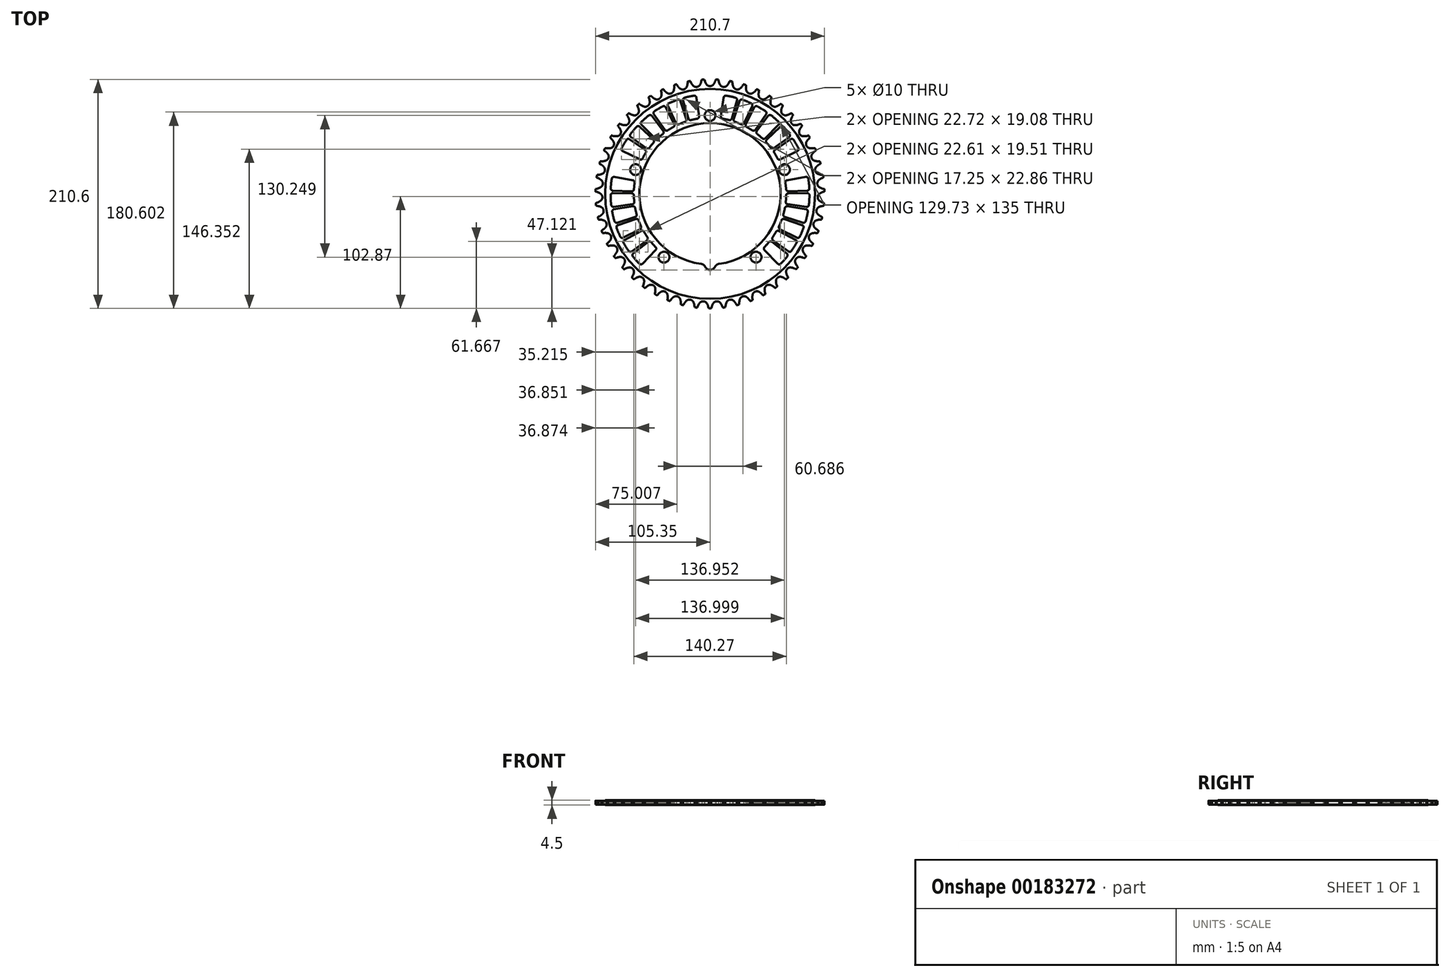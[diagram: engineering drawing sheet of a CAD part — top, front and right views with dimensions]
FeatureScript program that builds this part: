
annotation { "Feature Type Name" : "Feature", "Feature Type Description" : "" }
export const myFeature = defineFeature(function(context is Context, id is Id, definition is map)
    precondition{}
    {
        {
            var Q0;
            Q0=qCreatedBy(makeId("Top.planeOp"),FACE);
            var sketch = newSketch(context, id + "F0", { "sketchPlane" : qUnion([Q0])});
            skCircle(sketch, "E0", {"center": v(0, 0) * mm, "radius": 103.08 * mm, "construction": true});
            skArc(sketch, "E1", {"start": v(-4.68, 103.4) * mm, "mid": v(-4.06, 102) * mm, "end": v(-3.24, 100.71) * mm});
            skLineSegment(sketch, "E2", {"start": v(-4.68, 103.4) * mm, "end": v(-5.06, 104.51) * mm});
            skArc(sketch, "E3.trimOffspring", {"start": v(-5.06, 104.51) * mm, "mid": v(-5.7, 105.82) * mm, "end": v(-6.6, 106.94) * mm});
            skLineSegment(sketch, "E4.trimOffspring", {"start": v(0, 103.08) * mm, "end": v(0, 103.08) * mm});
            skArc(sketch, "E5.trimOffspring", {"start": v(-3.24, 100.71) * mm, "mid": v(-1.82, 99.5) * mm, "end": v(0, 99.07) * mm});
            skArc(sketch, "E6.MirrorCS", {"start": v(3.24, 100.71) * mm, "mid": v(1.82, 99.5) * mm, "end": v(0, 99.07) * mm});
            skArc(sketch, "E7.MirrorCS", {"start": v(4.68, 103.4) * mm, "mid": v(4.06, 102) * mm, "end": v(3.24, 100.71) * mm});
            skLineSegment(sketch, "E8.MirrorCS", {"start": v(4.68, 103.4) * mm, "end": v(5.06, 104.51) * mm});
            skArc(sketch, "E9.MirrorCS", {"start": v(5.06, 104.51) * mm, "mid": v(5.7, 105.82) * mm, "end": v(6.6, 106.94) * mm});
            skArc(sketch, "E10.1.0", {"start": v(-17.87, 103.1) * mm, "mid": v(-18.65, 104.31) * mm, "end": v(-19.69, 105.32) * mm});
            skLineSegment(sketch, "E10.1.1", {"start": v(-17.35, 102.05) * mm, "end": v(-17.87, 103.1) * mm});
            skArc(sketch, "E10.1.2", {"start": v(-17.35, 102.05) * mm, "mid": v(-16.56, 100.74) * mm, "end": v(-15.6, 99.55) * mm});
            skArc(sketch, "E10.1.3", {"start": v(-15.6, 99.55) * mm, "mid": v(-14.03, 98.53) * mm, "end": v(-12.17, 98.32) * mm});
            skArc(sketch, "E10.1.4", {"start": v(-9.16, 100.35) * mm, "mid": v(-10.42, 98.97) * mm, "end": v(-12.17, 98.32) * mm});
            skArc(sketch, "E10.1.5", {"start": v(-8.07, 103.2) * mm, "mid": v(-8.5, 101.73) * mm, "end": v(-9.16, 100.35) * mm});
            skLineSegment(sketch, "E10.1.6", {"start": v(-8.07, 103.2) * mm, "end": v(-7.82, 104.34) * mm});
            skArc(sketch, "E10.1.7", {"start": v(-7.82, 104.34) * mm, "mid": v(-7.36, 105.71) * mm, "end": v(-6.6, 106.94) * mm});
            skArc(sketch, "E10.2.0", {"start": v(-30.4, 100.12) * mm, "mid": v(-31.33, 101.23) * mm, "end": v(-32.48, 102.1) * mm});
            skLineSegment(sketch, "E10.2.1", {"start": v(-29.76, 99.14) * mm, "end": v(-30.4, 100.12) * mm});
            skArc(sketch, "E10.2.2", {"start": v(-29.76, 99.14) * mm, "mid": v(-28.82, 97.94) * mm, "end": v(-27.7, 96.88) * mm});
            skArc(sketch, "E10.2.3", {"start": v(-27.7, 96.88) * mm, "mid": v(-26.03, 96.06) * mm, "end": v(-24.16, 96.08) * mm});
            skArc(sketch, "E10.2.4", {"start": v(-21.42, 98.46) * mm, "mid": v(-22.5, 96.94) * mm, "end": v(-24.16, 96.08) * mm});
            skArc(sketch, "E10.2.5", {"start": v(-20.69, 101.43) * mm, "mid": v(-20.95, 99.92) * mm, "end": v(-21.42, 98.46) * mm});
            skLineSegment(sketch, "E10.2.6", {"start": v(-20.69, 101.43) * mm, "end": v(-20.58, 102.6) * mm});
            skArc(sketch, "E10.2.7", {"start": v(-20.58, 102.6) * mm, "mid": v(-20.3, 104) * mm, "end": v(-19.69, 105.32) * mm});
            skArc(sketch, "E10.3.0", {"start": v(-42.48, 95.63) * mm, "mid": v(-43.53, 96.61) * mm, "end": v(-44.78, 97.34) * mm});
            skLineSegment(sketch, "E10.3.1", {"start": v(-41.72, 94.74) * mm, "end": v(-42.48, 95.63) * mm});
            skArc(sketch, "E10.3.2", {"start": v(-41.72, 94.74) * mm, "mid": v(-40.63, 93.65) * mm, "end": v(-39.4, 92.74) * mm});
            skArc(sketch, "E10.3.3", {"start": v(-39.4, 92.74) * mm, "mid": v(-37.64, 92.13) * mm, "end": v(-35.79, 92.38) * mm});
            skArc(sketch, "E10.3.4", {"start": v(-33.36, 95.08) * mm, "mid": v(-34.25, 93.44) * mm, "end": v(-35.79, 92.38) * mm});
            skArc(sketch, "E10.3.5", {"start": v(-33, 98.11) * mm, "mid": v(-33.07, 96.59) * mm, "end": v(-33.36, 95.08) * mm});
            skLineSegment(sketch, "E10.3.6", {"start": v(-33, 98.11) * mm, "end": v(-33.03, 99.29) * mm});
            skArc(sketch, "E10.3.7", {"start": v(-33.03, 99.29) * mm, "mid": v(-32.92, 100.73) * mm, "end": v(-32.48, 102.1) * mm});
            skArc(sketch, "E10.4.0", {"start": v(-53.9, 89.68) * mm, "mid": v(-55.08, 90.53) * mm, "end": v(-56.4, 91.1) * mm});
            skLineSegment(sketch, "E10.4.1", {"start": v(-53.04, 88.9) * mm, "end": v(-53.9, 89.68) * mm});
            skArc(sketch, "E10.4.2", {"start": v(-53.04, 88.9) * mm, "mid": v(-51.83, 87.95) * mm, "end": v(-50.5, 87.2) * mm});
            skArc(sketch, "E10.4.3", {"start": v(-50.5, 87.2) * mm, "mid": v(-48.68, 86.8) * mm, "end": v(-46.87, 87.28) * mm});
            skArc(sketch, "E10.4.4", {"start": v(-44.8, 90.26) * mm, "mid": v(-45.47, 88.52) * mm, "end": v(-46.87, 87.28) * mm});
            skArc(sketch, "E10.4.5", {"start": v(-44.8, 93.32) * mm, "mid": v(-44.68, 91.8) * mm, "end": v(-44.8, 90.26) * mm});
            skLineSegment(sketch, "E10.4.6", {"start": v(-44.8, 93.32) * mm, "end": v(-44.98, 94.47) * mm});
            skArc(sketch, "E10.4.7", {"start": v(-44.98, 94.47) * mm, "mid": v(-45.05, 95.92) * mm, "end": v(-44.78, 97.34) * mm});
            skArc(sketch, "E10.5.0", {"start": v(-64.52, 82.38) * mm, "mid": v(-65.78, 83.08) * mm, "end": v(-67.17, 83.48) * mm});
            skLineSegment(sketch, "E10.5.1", {"start": v(-63.56, 81.7) * mm, "end": v(-64.52, 82.38) * mm});
            skArc(sketch, "E10.5.2", {"start": v(-63.56, 81.7) * mm, "mid": v(-62.25, 80.91) * mm, "end": v(-60.84, 80.33) * mm});
            skArc(sketch, "E10.5.3", {"start": v(-60.84, 80.33) * mm, "mid": v(-58.97, 80.17) * mm, "end": v(-57.24, 80.86) * mm});
            skArc(sketch, "E10.5.4", {"start": v(-55.54, 84.08) * mm, "mid": v(-56, 82.27) * mm, "end": v(-57.24, 80.86) * mm});
            skArc(sketch, "E10.5.5", {"start": v(-55.93, 87.1) * mm, "mid": v(-55.63, 85.6) * mm, "end": v(-55.54, 84.08) * mm});
            skLineSegment(sketch, "E10.5.6", {"start": v(-55.93, 87.1) * mm, "end": v(-56.25, 88.23) * mm});
            skArc(sketch, "E10.5.7", {"start": v(-56.25, 88.23) * mm, "mid": v(-56.5, 89.66) * mm, "end": v(-56.4, 91.1) * mm});
            skArc(sketch, "E10.6.0", {"start": v(-74.15, 73.83) * mm, "mid": v(-75.5, 74.36) * mm, "end": v(-76.92, 74.59) * mm});
            skLineSegment(sketch, "E10.6.1", {"start": v(-73.12, 73.27) * mm, "end": v(-74.15, 73.83) * mm});
            skArc(sketch, "E10.6.2", {"start": v(-73.12, 73.27) * mm, "mid": v(-71.72, 72.65) * mm, "end": v(-70.25, 72.25) * mm});
            skArc(sketch, "E10.6.3", {"start": v(-70.25, 72.25) * mm, "mid": v(-68.38, 72.31) * mm, "end": v(-66.74, 73.21) * mm});
            skArc(sketch, "E10.6.4", {"start": v(-65.46, 76.61) * mm, "mid": v(-65.7, 74.76) * mm, "end": v(-66.74, 73.21) * mm});
            skArc(sketch, "E10.6.5", {"start": v(-66.2, 79.57) * mm, "mid": v(-65.72, 78.12) * mm, "end": v(-65.46, 76.61) * mm});
            skLineSegment(sketch, "E10.6.6", {"start": v(-66.2, 79.57) * mm, "end": v(-66.67, 80.65) * mm});
            skArc(sketch, "E10.6.7", {"start": v(-66.67, 80.65) * mm, "mid": v(-67.08, 82.03) * mm, "end": v(-67.17, 83.48) * mm});
            skArc(sketch, "E10.7.0", {"start": v(-82.66, 64.15) * mm, "mid": v(-84.06, 64.52) * mm, "end": v(-85.5, 64.57) * mm});
            skLineSegment(sketch, "E10.7.1", {"start": v(-81.57, 63.73) * mm, "end": v(-82.66, 64.15) * mm});
            skArc(sketch, "E10.7.2", {"start": v(-81.57, 63.73) * mm, "mid": v(-80.1, 63.29) * mm, "end": v(-78.6, 63.07) * mm});
            skArc(sketch, "E10.7.3", {"start": v(-78.6, 63.07) * mm, "mid": v(-76.75, 63.36) * mm, "end": v(-75.23, 64.46) * mm});
            skArc(sketch, "E10.7.4", {"start": v(-74.37, 67.99) * mm, "mid": v(-74.38, 66.12) * mm, "end": v(-75.23, 64.46) * mm});
            skArc(sketch, "E10.7.5", {"start": v(-75.49, 70.83) * mm, "mid": v(-74.83, 69.45) * mm, "end": v(-74.37, 67.99) * mm});
            skLineSegment(sketch, "E10.7.6", {"start": v(-75.49, 70.83) * mm, "end": v(-76.07, 71.84) * mm});
            skArc(sketch, "E10.7.7", {"start": v(-76.07, 71.84) * mm, "mid": v(-76.65, 73.17) * mm, "end": v(-76.92, 74.59) * mm});
            skArc(sketch, "E10.8.0", {"start": v(-89.92, 53.5) * mm, "mid": v(-91.35, 53.7) * mm, "end": v(-92.8, 53.57) * mm});
            skLineSegment(sketch, "E10.8.1", {"start": v(-88.78, 53.22) * mm, "end": v(-89.92, 53.5) * mm});
            skArc(sketch, "E10.8.2", {"start": v(-88.78, 53.22) * mm, "mid": v(-87.28, 52.96) * mm, "end": v(-85.75, 52.93) * mm});
            skArc(sketch, "E10.8.3", {"start": v(-85.75, 52.93) * mm, "mid": v(-83.95, 53.45) * mm, "end": v(-82.58, 54.72) * mm});
            skArc(sketch, "E10.8.4", {"start": v(-82.17, 58.33) * mm, "mid": v(-81.94, 56.48) * mm, "end": v(-82.58, 54.72) * mm});
            skArc(sketch, "E10.8.5", {"start": v(-83.62, 61.02) * mm, "mid": v(-82.8, 59.73) * mm, "end": v(-82.17, 58.33) * mm});
            skLineSegment(sketch, "E10.8.6", {"start": v(-83.62, 61.02) * mm, "end": v(-84.33, 61.95) * mm});
            skArc(sketch, "E10.8.7", {"start": v(-84.33, 61.95) * mm, "mid": v(-85.06, 63.2) * mm, "end": v(-85.5, 64.57) * mm});
            skArc(sketch, "E10.9.0", {"start": v(-95.81, 42.05) * mm, "mid": v(-97.26, 42.07) * mm, "end": v(-98.67, 41.76) * mm});
            skLineSegment(sketch, "E10.9.1", {"start": v(-94.65, 41.9) * mm, "end": v(-95.81, 42.05) * mm});
            skArc(sketch, "E10.9.2", {"start": v(-94.65, 41.9) * mm, "mid": v(-93.12, 41.84) * mm, "end": v(-91.6, 42) * mm});
            skArc(sketch, "E10.9.3", {"start": v(-91.6, 42) * mm, "mid": v(-89.88, 42.73) * mm, "end": v(-88.68, 44.16) * mm});
            skArc(sketch, "E10.9.4", {"start": v(-88.71, 47.8) * mm, "mid": v(-88.26, 45.98) * mm, "end": v(-88.68, 44.16) * mm});
            skArc(sketch, "E10.9.5", {"start": v(-90.48, 50.28) * mm, "mid": v(-89.5, 49.1) * mm, "end": v(-88.71, 47.8) * mm});
            skLineSegment(sketch, "E10.9.6", {"start": v(-90.48, 50.28) * mm, "end": v(-91.3, 51.12) * mm});
            skArc(sketch, "E10.9.7", {"start": v(-91.3, 51.12) * mm, "mid": v(-92.19, 52.26) * mm, "end": v(-92.8, 53.57) * mm});
            skArc(sketch, "E10.10.0", {"start": v(-100.26, 29.96) * mm, "mid": v(-101.7, 29.8) * mm, "end": v(-103.06, 29.32) * mm});
            skLineSegment(sketch, "E10.10.1", {"start": v(-99.08, 29.96) * mm, "end": v(-100.26, 29.96) * mm});
            skArc(sketch, "E10.10.2", {"start": v(-99.08, 29.96) * mm, "mid": v(-97.56, 30.08) * mm, "end": v(-96.07, 30.42) * mm});
            skArc(sketch, "E10.10.3", {"start": v(-96.07, 30.42) * mm, "mid": v(-94.45, 31.36) * mm, "end": v(-93.44, 32.93) * mm});
            skArc(sketch, "E10.10.4", {"start": v(-93.91, 36.53) * mm, "mid": v(-93.24, 34.78) * mm, "end": v(-93.44, 32.93) * mm});
            skArc(sketch, "E10.10.5", {"start": v(-95.98, 38.78) * mm, "mid": v(-94.86, 37.73) * mm, "end": v(-93.91, 36.53) * mm});
            skLineSegment(sketch, "E10.10.6", {"start": v(-95.98, 38.78) * mm, "end": v(-96.89, 39.51) * mm});
            skArc(sketch, "E10.10.7", {"start": v(-96.89, 39.51) * mm, "mid": v(-97.9, 40.54) * mm, "end": v(-98.67, 41.76) * mm});
            skArc(sketch, "E10.11.0", {"start": v(-103.18, 17.41) * mm, "mid": v(-104.58, 17.08) * mm, "end": v(-105.88, 16.44) * mm});
            skLineSegment(sketch, "E10.11.1", {"start": v(-102.01, 17.55) * mm, "end": v(-103.18, 17.41) * mm});
            skArc(sketch, "E10.11.2", {"start": v(-102.01, 17.55) * mm, "mid": v(-100.51, 17.86) * mm, "end": v(-99.08, 18.38) * mm});
            skArc(sketch, "E10.11.3", {"start": v(-99.08, 18.38) * mm, "mid": v(-97.59, 19.51) * mm, "end": v(-96.78, 21.2) * mm});
            skArc(sketch, "E10.11.4", {"start": v(-97.69, 24.71) * mm, "mid": v(-96.81, 23.06) * mm, "end": v(-96.78, 21.2) * mm});
            skArc(sketch, "E10.11.5", {"start": v(-100.01, 26.7) * mm, "mid": v(-98.78, 25.79) * mm, "end": v(-97.69, 24.71) * mm});
            skLineSegment(sketch, "E10.11.6", {"start": v(-100.01, 26.7) * mm, "end": v(-101.01, 27.3) * mm});
            skArc(sketch, "E10.11.7", {"start": v(-101.01, 27.3) * mm, "mid": v(-102.15, 28.2) * mm, "end": v(-103.06, 29.32) * mm});
            skArc(sketch, "E10.12.0", {"start": v(-104.54, 4.6) * mm, "mid": v(-105.89, 4.1) * mm, "end": v(-107.1, 3.3) * mm});
            skLineSegment(sketch, "E10.12.1", {"start": v(-103.4, 4.88) * mm, "end": v(-104.54, 4.6) * mm});
            skArc(sketch, "E10.12.2", {"start": v(-103.4, 4.88) * mm, "mid": v(-101.95, 5.37) * mm, "end": v(-100.58, 6.07) * mm});
            skArc(sketch, "E10.12.3", {"start": v(-100.58, 6.07) * mm, "mid": v(-99.25, 7.37) * mm, "end": v(-98.65, 9.14) * mm});
            skArc(sketch, "E10.12.4", {"start": v(-99.99, 12.52) * mm, "mid": v(-98.91, 11) * mm, "end": v(-98.65, 9.14) * mm});
            skArc(sketch, "E10.12.5", {"start": v(-102.54, 14.2) * mm, "mid": v(-101.2, 13.45) * mm, "end": v(-99.99, 12.52) * mm});
            skLineSegment(sketch, "E10.12.6", {"start": v(-102.54, 14.2) * mm, "end": v(-103.6, 14.69) * mm});
            skArc(sketch, "E10.12.7", {"start": v(-103.6, 14.69) * mm, "mid": v(-104.84, 15.43) * mm, "end": v(-105.88, 16.44) * mm});
            skArc(sketch, "E10.13.0", {"start": v(-104.3, -8.28) * mm, "mid": v(-105.6, -8.95) * mm, "end": v(-106.7, -9.89) * mm});
            skLineSegment(sketch, "E10.13.1", {"start": v(-103.22, -7.86) * mm, "end": v(-104.3, -8.28) * mm});
            skArc(sketch, "E10.13.2", {"start": v(-103.22, -7.86) * mm, "mid": v(-101.84, -7.2) * mm, "end": v(-100.57, -6.34) * mm});
            skArc(sketch, "E10.13.3", {"start": v(-100.57, -6.34) * mm, "mid": v(-99.4, -4.88) * mm, "end": v(-99.02, -3.05) * mm});
            skArc(sketch, "E10.13.4", {"start": v(-100.77, 0.14) * mm, "mid": v(-99.51, -1.25) * mm, "end": v(-99.02, -3.05) * mm});
            skArc(sketch, "E10.13.5", {"start": v(-103.5, 1.5) * mm, "mid": v(-102.08, 0.92) * mm, "end": v(-100.77, 0.14) * mm});
            skLineSegment(sketch, "E10.13.6", {"start": v(-103.5, 1.5) * mm, "end": v(-104.62, 1.84) * mm});
            skArc(sketch, "E10.13.7", {"start": v(-104.62, 1.84) * mm, "mid": v(-105.94, 2.43) * mm, "end": v(-107.1, 3.3) * mm});
            skArc(sketch, "E10.14.0", {"start": v(-102.5, -21.03) * mm, "mid": v(-103.7, -21.86) * mm, "end": v(-104.67, -22.92) * mm});
            skLineSegment(sketch, "E10.14.1", {"start": v(-101.47, -20.48) * mm, "end": v(-102.5, -21.03) * mm});
            skArc(sketch, "E10.14.2", {"start": v(-101.47, -20.48) * mm, "mid": v(-100.18, -19.66) * mm, "end": v(-99.03, -18.65) * mm});
            skArc(sketch, "E10.14.3", {"start": v(-99.03, -18.65) * mm, "mid": v(-98.05, -17.06) * mm, "end": v(-97.9, -15.2) * mm});
            skArc(sketch, "E10.14.4", {"start": v(-100.02, -12.25) * mm, "mid": v(-98.6, -13.47) * mm, "end": v(-97.9, -15.2) * mm});
            skArc(sketch, "E10.14.5", {"start": v(-102.9, -11.24) * mm, "mid": v(-101.42, -11.64) * mm, "end": v(-100.02, -12.25) * mm});
            skLineSegment(sketch, "E10.14.6", {"start": v(-102.9, -11.24) * mm, "end": v(-104.05, -11.03) * mm});
            skArc(sketch, "E10.14.7", {"start": v(-104.05, -11.03) * mm, "mid": v(-105.44, -10.6) * mm, "end": v(-106.7, -9.89) * mm});
            skArc(sketch, "E10.15.0", {"start": v(-99.14, -33.47) * mm, "mid": v(-100.22, -34.43) * mm, "end": v(-101.06, -35.61) * mm});
            skLineSegment(sketch, "E10.15.1", {"start": v(-98.18, -32.8) * mm, "end": v(-99.14, -33.47) * mm});
            skArc(sketch, "E10.15.2", {"start": v(-98.18, -32.8) * mm, "mid": v(-97, -31.82) * mm, "end": v(-95.98, -30.68) * mm});
            skArc(sketch, "E10.15.3", {"start": v(-95.98, -30.68) * mm, "mid": v(-95.2, -28.98) * mm, "end": v(-95.29, -27.11) * mm});
            skArc(sketch, "E10.15.4", {"start": v(-97.76, -24.44) * mm, "mid": v(-96.2, -25.48) * mm, "end": v(-95.29, -27.11) * mm});
            skArc(sketch, "E10.15.5", {"start": v(-100.74, -23.8) * mm, "mid": v(-99.22, -24.01) * mm, "end": v(-97.76, -24.44) * mm});
            skLineSegment(sketch, "E10.15.6", {"start": v(-100.74, -23.8) * mm, "end": v(-101.9, -23.73) * mm});
            skArc(sketch, "E10.15.7", {"start": v(-101.9, -23.73) * mm, "mid": v(-103.33, -23.48) * mm, "end": v(-104.67, -22.92) * mm});
            skArc(sketch, "E10.16.0", {"start": v(-94.27, -45.4) * mm, "mid": v(-95.23, -46.49) * mm, "end": v(-95.91, -47.76) * mm});
            skLineSegment(sketch, "E10.16.1", {"start": v(-93.4, -44.61) * mm, "end": v(-94.27, -45.4) * mm});
            skArc(sketch, "E10.16.2", {"start": v(-93.4, -44.61) * mm, "mid": v(-92.36, -43.5) * mm, "end": v(-91.49, -42.24) * mm});
            skArc(sketch, "E10.16.3", {"start": v(-91.49, -42.24) * mm, "mid": v(-90.93, -40.46) * mm, "end": v(-91.23, -38.62) * mm});
            skArc(sketch, "E10.16.4", {"start": v(-94.01, -36.27) * mm, "mid": v(-92.34, -37.11) * mm, "end": v(-91.23, -38.62) * mm});
            skArc(sketch, "E10.16.5", {"start": v(-97.05, -36) * mm, "mid": v(-95.52, -36.02) * mm, "end": v(-94.01, -36.27) * mm});
            skLineSegment(sketch, "E10.16.6", {"start": v(-97.05, -36) * mm, "end": v(-98.22, -36.08) * mm});
            skArc(sketch, "E10.16.7", {"start": v(-98.22, -36.08) * mm, "mid": v(-99.67, -36) * mm, "end": v(-101.06, -35.61) * mm});
            skArc(sketch, "E10.17.0", {"start": v(-87.98, -56.64) * mm, "mid": v(-88.8, -57.84) * mm, "end": v(-89.32, -59.18) * mm});
            skLineSegment(sketch, "E10.17.1", {"start": v(-87.22, -55.75) * mm, "end": v(-87.98, -56.64) * mm});
            skArc(sketch, "E10.17.2", {"start": v(-87.22, -55.75) * mm, "mid": v(-86.31, -54.52) * mm, "end": v(-85.6, -53.16) * mm});
            skArc(sketch, "E10.17.3", {"start": v(-85.6, -53.16) * mm, "mid": v(-85.26, -51.33) * mm, "end": v(-85.8, -49.53) * mm});
            skArc(sketch, "E10.17.4", {"start": v(-88.84, -47.55) * mm, "mid": v(-87.08, -48.18) * mm, "end": v(-85.8, -49.53) * mm});
            skArc(sketch, "E10.17.5", {"start": v(-91.9, -47.65) * mm, "mid": v(-90.37, -47.49) * mm, "end": v(-88.84, -47.55) * mm});
            skLineSegment(sketch, "E10.17.6", {"start": v(-91.9, -47.65) * mm, "end": v(-93.04, -47.87) * mm});
            skArc(sketch, "E10.17.7", {"start": v(-93.04, -47.87) * mm, "mid": v(-94.49, -47.98) * mm, "end": v(-95.91, -47.76) * mm});
            skArc(sketch, "E10.18.0", {"start": v(-80.35, -67.02) * mm, "mid": v(-81.01, -68.31) * mm, "end": v(-81.37, -69.71) * mm});
            skLineSegment(sketch, "E10.18.1", {"start": v(-79.7, -66.05) * mm, "end": v(-80.35, -67.02) * mm});
            skArc(sketch, "E10.18.2", {"start": v(-79.7, -66.05) * mm, "mid": v(-78.96, -64.71) * mm, "end": v(-78.42, -63.28) * mm});
            skArc(sketch, "E10.18.3", {"start": v(-78.42, -63.28) * mm, "mid": v(-78.31, -61.42) * mm, "end": v(-79.06, -59.7) * mm});
            skArc(sketch, "E10.18.4", {"start": v(-82.33, -58.1) * mm, "mid": v(-80.5, -58.51) * mm, "end": v(-79.06, -59.7) * mm});
            skArc(sketch, "E10.18.5", {"start": v(-85.34, -58.59) * mm, "mid": v(-83.85, -58.24) * mm, "end": v(-82.33, -58.1) * mm});
            skLineSegment(sketch, "E10.18.6", {"start": v(-85.34, -58.59) * mm, "end": v(-86.46, -58.94) * mm});
            skArc(sketch, "E10.18.7", {"start": v(-86.46, -58.94) * mm, "mid": v(-87.87, -59.23) * mm, "end": v(-89.32, -59.18) * mm});
            skArc(sketch, "E10.19.0", {"start": v(-71.5, -76.4) * mm, "mid": v(-72, -77.75) * mm, "end": v(-72.18, -79.18) * mm});
            skLineSegment(sketch, "E10.19.1", {"start": v(-70.98, -75.34) * mm, "end": v(-71.5, -76.4) * mm});
            skArc(sketch, "E10.19.2", {"start": v(-70.98, -75.34) * mm, "mid": v(-70.4, -73.93) * mm, "end": v(-70.05, -72.44) * mm});
            skArc(sketch, "E10.19.3", {"start": v(-70.05, -72.44) * mm, "mid": v(-70.17, -70.57) * mm, "end": v(-71.12, -68.97) * mm});
            skArc(sketch, "E10.19.4", {"start": v(-74.56, -67.78) * mm, "mid": v(-72.7, -67.96) * mm, "end": v(-71.12, -68.97) * mm});
            skArc(sketch, "E10.19.5", {"start": v(-77.5, -68.63) * mm, "mid": v(-76.06, -68.1) * mm, "end": v(-74.56, -67.78) * mm});
            skLineSegment(sketch, "E10.19.6", {"start": v(-77.5, -68.63) * mm, "end": v(-78.56, -69.12) * mm});
            skArc(sketch, "E10.19.7", {"start": v(-78.56, -69.12) * mm, "mid": v(-79.93, -69.58) * mm, "end": v(-81.37, -69.71) * mm});
            skArc(sketch, "E10.20.0", {"start": v(-61.58, -84.6) * mm, "mid": v(-61.9, -86) * mm, "end": v(-61.9, -87.45) * mm});
            skLineSegment(sketch, "E10.20.1", {"start": v(-61.19, -83.5) * mm, "end": v(-61.58, -84.6) * mm});
            skArc(sketch, "E10.20.2", {"start": v(-61.19, -83.5) * mm, "mid": v(-60.79, -82.02) * mm, "end": v(-60.62, -80.5) * mm});
            skArc(sketch, "E10.20.3", {"start": v(-60.62, -80.5) * mm, "mid": v(-60.97, -78.66) * mm, "end": v(-62.1, -77.18) * mm});
            skArc(sketch, "E10.20.4", {"start": v(-65.67, -76.43) * mm, "mid": v(-63.8, -76.38) * mm, "end": v(-62.1, -77.18) * mm});
            skArc(sketch, "E10.20.5", {"start": v(-68.47, -77.63) * mm, "mid": v(-67.11, -76.93) * mm, "end": v(-65.67, -76.43) * mm});
            skLineSegment(sketch, "E10.20.6", {"start": v(-68.47, -77.63) * mm, "end": v(-69.47, -78.25) * mm});
            skArc(sketch, "E10.20.7", {"start": v(-69.47, -78.25) * mm, "mid": v(-70.77, -78.87) * mm, "end": v(-72.18, -79.18) * mm});
            skArc(sketch, "E10.21.0", {"start": v(-50.71, -91.52) * mm, "mid": v(-50.87, -92.96) * mm, "end": v(-50.7, -94.4) * mm});
            skLineSegment(sketch, "E10.21.1", {"start": v(-50.46, -90.38) * mm, "end": v(-50.71, -91.52) * mm});
            skArc(sketch, "E10.21.2", {"start": v(-50.46, -90.38) * mm, "mid": v(-50.25, -88.87) * mm, "end": v(-50.26, -87.34) * mm});
            skArc(sketch, "E10.21.3", {"start": v(-50.26, -87.34) * mm, "mid": v(-50.84, -85.56) * mm, "end": v(-52.15, -84.23) * mm});
            skArc(sketch, "E10.21.4", {"start": v(-55.78, -83.92) * mm, "mid": v(-53.93, -83.64) * mm, "end": v(-52.15, -84.23) * mm});
            skArc(sketch, "E10.21.5", {"start": v(-58.41, -85.46) * mm, "mid": v(-57.15, -84.6) * mm, "end": v(-55.78, -83.92) * mm});
            skLineSegment(sketch, "E10.21.6", {"start": v(-58.41, -85.46) * mm, "end": v(-59.32, -86.2) * mm});
            skArc(sketch, "E10.21.7", {"start": v(-59.32, -86.2) * mm, "mid": v(-60.54, -86.97) * mm, "end": v(-61.9, -87.45) * mm});
            skArc(sketch, "E10.22.0", {"start": v(-39.08, -97.06) * mm, "mid": v(-39.06, -98.5) * mm, "end": v(-38.7, -99.91) * mm});
            skLineSegment(sketch, "E10.22.1", {"start": v(-38.97, -95.9) * mm, "end": v(-39.08, -97.06) * mm});
            skArc(sketch, "E10.22.2", {"start": v(-38.97, -95.9) * mm, "mid": v(-38.95, -94.37) * mm, "end": v(-39.15, -92.85) * mm});
            skArc(sketch, "E10.22.3", {"start": v(-39.15, -92.85) * mm, "mid": v(-39.94, -91.16) * mm, "end": v(-41.4, -90) * mm});
            skArc(sketch, "E10.22.4", {"start": v(-45.04, -90.14) * mm, "mid": v(-43.24, -89.64) * mm, "end": v(-41.4, -90) * mm});
            skArc(sketch, "E10.22.5", {"start": v(-47.47, -91.99) * mm, "mid": v(-46.32, -90.97) * mm, "end": v(-45.04, -90.14) * mm});
            skLineSegment(sketch, "E10.22.6", {"start": v(-47.47, -91.99) * mm, "end": v(-48.28, -92.83) * mm});
            skArc(sketch, "E10.22.7", {"start": v(-48.28, -92.83) * mm, "mid": v(-49.4, -93.75) * mm, "end": v(-50.7, -94.4) * mm});
            skArc(sketch, "E10.23.0", {"start": v(-26.86, -101.13) * mm, "mid": v(-26.65, -102.56) * mm, "end": v(-26.13, -103.91) * mm});
            skLineSegment(sketch, "E10.23.1", {"start": v(-26.9, -99.96) * mm, "end": v(-26.86, -101.13) * mm});
            skArc(sketch, "E10.23.2", {"start": v(-26.9, -99.96) * mm, "mid": v(-27.06, -98.44) * mm, "end": v(-27.44, -96.96) * mm});
            skArc(sketch, "E10.23.3", {"start": v(-27.44, -96.96) * mm, "mid": v(-28.43, -95.37) * mm, "end": v(-30.03, -94.4) * mm});
            skArc(sketch, "E10.23.4", {"start": v(-33.62, -95) * mm, "mid": v(-31.9, -94.27) * mm, "end": v(-30.03, -94.4) * mm});
            skArc(sketch, "E10.23.5", {"start": v(-35.8, -97.12) * mm, "mid": v(-34.8, -95.98) * mm, "end": v(-33.62, -95) * mm});
            skLineSegment(sketch, "E10.23.6", {"start": v(-35.8, -97.12) * mm, "end": v(-36.5, -98.06) * mm});
            skArc(sketch, "E10.23.7", {"start": v(-36.5, -98.06) * mm, "mid": v(-37.5, -99.11) * mm, "end": v(-38.7, -99.91) * mm});
            skArc(sketch, "E10.24.0", {"start": v(-14.23, -103.66) * mm, "mid": v(-13.85, -105.06) * mm, "end": v(-13.17, -106.34) * mm});
            skLineSegment(sketch, "E10.24.1", {"start": v(-14.4, -102.5) * mm, "end": v(-14.23, -103.66) * mm});
            skArc(sketch, "E10.24.2", {"start": v(-14.4, -102.5) * mm, "mid": v(-14.75, -101.02) * mm, "end": v(-15.32, -99.6) * mm});
            skArc(sketch, "E10.24.3", {"start": v(-15.32, -99.6) * mm, "mid": v(-16.5, -98.14) * mm, "end": v(-18.2, -97.38) * mm});
            skArc(sketch, "E10.24.4", {"start": v(-21.7, -98.4) * mm, "mid": v(-20.07, -97.48) * mm, "end": v(-18.2, -97.38) * mm});
            skArc(sketch, "E10.24.5", {"start": v(-23.6, -100.79) * mm, "mid": v(-22.73, -99.53) * mm, "end": v(-21.7, -98.4) * mm});
            skLineSegment(sketch, "E10.24.6", {"start": v(-23.6, -100.79) * mm, "end": v(-24.18, -101.8) * mm});
            skArc(sketch, "E10.24.7", {"start": v(-24.18, -101.8) * mm, "mid": v(-25.04, -102.97) * mm, "end": v(-26.13, -103.91) * mm});
            skArc(sketch, "E10.25.0", {"start": v(-1.38, -104.63) * mm, "mid": v(-0.83, -105.97) * mm, "end": v(0, -107.15) * mm});
            skLineSegment(sketch, "E10.25.1", {"start": v(-1.7, -103.5) * mm, "end": v(-1.38, -104.63) * mm});
            skArc(sketch, "E10.25.2", {"start": v(-1.7, -103.5) * mm, "mid": v(-2.23, -102.06) * mm, "end": v(-2.97, -100.72) * mm});
            skArc(sketch, "E10.25.3", {"start": v(-2.97, -100.72) * mm, "mid": v(-4.31, -99.43) * mm, "end": v(-6.1, -98.88) * mm});
            skArc(sketch, "E10.25.4", {"start": v(-9.44, -100.32) * mm, "mid": v(-7.94, -99.2) * mm, "end": v(-6.1, -98.88) * mm});
            skArc(sketch, "E10.25.5", {"start": v(-11.03, -102.92) * mm, "mid": v(-10.33, -101.57) * mm, "end": v(-9.44, -100.32) * mm});
            skLineSegment(sketch, "E10.25.6", {"start": v(-11.03, -102.92) * mm, "end": v(-11.49, -104) * mm});
            skArc(sketch, "E10.25.7", {"start": v(-11.49, -104) * mm, "mid": v(-12.2, -105.26) * mm, "end": v(-13.17, -106.34) * mm});
            skArc(sketch, "E10.26.0", {"start": v(11.49, -104) * mm, "mid": v(12.2, -105.26) * mm, "end": v(13.17, -106.34) * mm});
            skLineSegment(sketch, "E10.26.1", {"start": v(11.03, -102.92) * mm, "end": v(11.49, -104) * mm});
            skArc(sketch, "E10.26.2", {"start": v(11.03, -102.92) * mm, "mid": v(10.33, -101.57) * mm, "end": v(9.44, -100.32) * mm});
            skArc(sketch, "E10.26.3", {"start": v(9.44, -100.32) * mm, "mid": v(7.94, -99.2) * mm, "end": v(6.1, -98.88) * mm});
            skArc(sketch, "E10.26.4", {"start": v(2.97, -100.72) * mm, "mid": v(4.31, -99.43) * mm, "end": v(6.1, -98.88) * mm});
            skArc(sketch, "E10.26.5", {"start": v(1.7, -103.5) * mm, "mid": v(2.23, -102.06) * mm, "end": v(2.97, -100.72) * mm});
            skLineSegment(sketch, "E10.26.6", {"start": v(1.7, -103.5) * mm, "end": v(1.38, -104.63) * mm});
            skArc(sketch, "E10.26.7", {"start": v(1.38, -104.63) * mm, "mid": v(0.83, -105.97) * mm, "end": v(0, -107.15) * mm});
            skArc(sketch, "E10.27.0", {"start": v(24.18, -101.8) * mm, "mid": v(25.04, -102.97) * mm, "end": v(26.13, -103.91) * mm});
            skLineSegment(sketch, "E10.27.1", {"start": v(23.6, -100.79) * mm, "end": v(24.18, -101.8) * mm});
            skArc(sketch, "E10.27.2", {"start": v(23.6, -100.79) * mm, "mid": v(22.73, -99.53) * mm, "end": v(21.7, -98.4) * mm});
            skArc(sketch, "E10.27.3", {"start": v(21.7, -98.4) * mm, "mid": v(20.07, -97.48) * mm, "end": v(18.2, -97.38) * mm});
            skArc(sketch, "E10.27.4", {"start": v(15.32, -99.6) * mm, "mid": v(16.5, -98.14) * mm, "end": v(18.2, -97.38) * mm});
            skArc(sketch, "E10.27.5", {"start": v(14.4, -102.5) * mm, "mid": v(14.75, -101.02) * mm, "end": v(15.32, -99.6) * mm});
            skLineSegment(sketch, "E10.27.6", {"start": v(14.4, -102.5) * mm, "end": v(14.23, -103.66) * mm});
            skArc(sketch, "E10.27.7", {"start": v(14.23, -103.66) * mm, "mid": v(13.85, -105.06) * mm, "end": v(13.17, -106.34) * mm});
            skArc(sketch, "E10.28.0", {"start": v(36.5, -98.06) * mm, "mid": v(37.5, -99.11) * mm, "end": v(38.7, -99.91) * mm});
            skLineSegment(sketch, "E10.28.1", {"start": v(35.8, -97.12) * mm, "end": v(36.5, -98.06) * mm});
            skArc(sketch, "E10.28.2", {"start": v(35.8, -97.12) * mm, "mid": v(34.8, -95.98) * mm, "end": v(33.62, -95) * mm});
            skArc(sketch, "E10.28.3", {"start": v(33.62, -95) * mm, "mid": v(31.9, -94.27) * mm, "end": v(30.03, -94.4) * mm});
            skArc(sketch, "E10.28.4", {"start": v(27.44, -96.96) * mm, "mid": v(28.43, -95.37) * mm, "end": v(30.03, -94.4) * mm});
            skArc(sketch, "E10.28.5", {"start": v(26.9, -99.96) * mm, "mid": v(27.06, -98.44) * mm, "end": v(27.44, -96.96) * mm});
            skLineSegment(sketch, "E10.28.6", {"start": v(26.9, -99.96) * mm, "end": v(26.86, -101.13) * mm});
            skArc(sketch, "E10.28.7", {"start": v(26.86, -101.13) * mm, "mid": v(26.65, -102.56) * mm, "end": v(26.13, -103.91) * mm});
            skArc(sketch, "E10.29.0", {"start": v(48.28, -92.83) * mm, "mid": v(49.4, -93.75) * mm, "end": v(50.7, -94.4) * mm});
            skLineSegment(sketch, "E10.29.1", {"start": v(47.47, -91.99) * mm, "end": v(48.28, -92.83) * mm});
            skArc(sketch, "E10.29.2", {"start": v(47.47, -91.99) * mm, "mid": v(46.32, -90.97) * mm, "end": v(45.04, -90.14) * mm});
            skArc(sketch, "E10.29.3", {"start": v(45.04, -90.14) * mm, "mid": v(43.24, -89.64) * mm, "end": v(41.4, -90) * mm});
            skArc(sketch, "E10.29.4", {"start": v(39.15, -92.85) * mm, "mid": v(39.94, -91.16) * mm, "end": v(41.4, -90) * mm});
            skArc(sketch, "E10.29.5", {"start": v(38.97, -95.9) * mm, "mid": v(38.95, -94.37) * mm, "end": v(39.15, -92.85) * mm});
            skLineSegment(sketch, "E10.29.6", {"start": v(38.97, -95.9) * mm, "end": v(39.08, -97.06) * mm});
            skArc(sketch, "E10.29.7", {"start": v(39.08, -97.06) * mm, "mid": v(39.06, -98.5) * mm, "end": v(38.7, -99.91) * mm});
            skArc(sketch, "E10.30.0", {"start": v(59.32, -86.2) * mm, "mid": v(60.54, -86.97) * mm, "end": v(61.9, -87.45) * mm});
            skLineSegment(sketch, "E10.30.1", {"start": v(58.41, -85.46) * mm, "end": v(59.32, -86.2) * mm});
            skArc(sketch, "E10.30.2", {"start": v(58.41, -85.46) * mm, "mid": v(57.15, -84.6) * mm, "end": v(55.78, -83.92) * mm});
            skArc(sketch, "E10.30.3", {"start": v(55.78, -83.92) * mm, "mid": v(53.93, -83.64) * mm, "end": v(52.15, -84.23) * mm});
            skArc(sketch, "E10.30.4", {"start": v(50.26, -87.34) * mm, "mid": v(50.84, -85.56) * mm, "end": v(52.15, -84.23) * mm});
            skArc(sketch, "E10.30.5", {"start": v(50.46, -90.38) * mm, "mid": v(50.25, -88.87) * mm, "end": v(50.26, -87.34) * mm});
            skLineSegment(sketch, "E10.30.6", {"start": v(50.46, -90.38) * mm, "end": v(50.71, -91.52) * mm});
            skArc(sketch, "E10.30.7", {"start": v(50.71, -91.52) * mm, "mid": v(50.87, -92.96) * mm, "end": v(50.7, -94.4) * mm});
            skArc(sketch, "E10.31.0", {"start": v(69.47, -78.25) * mm, "mid": v(70.77, -78.87) * mm, "end": v(72.18, -79.18) * mm});
            skLineSegment(sketch, "E10.31.1", {"start": v(68.47, -77.63) * mm, "end": v(69.47, -78.25) * mm});
            skArc(sketch, "E10.31.2", {"start": v(68.47, -77.63) * mm, "mid": v(67.11, -76.93) * mm, "end": v(65.67, -76.43) * mm});
            skArc(sketch, "E10.31.3", {"start": v(65.67, -76.43) * mm, "mid": v(63.8, -76.38) * mm, "end": v(62.1, -77.18) * mm});
            skArc(sketch, "E10.31.4", {"start": v(60.62, -80.5) * mm, "mid": v(60.97, -78.66) * mm, "end": v(62.1, -77.18) * mm});
            skArc(sketch, "E10.31.5", {"start": v(61.19, -83.5) * mm, "mid": v(60.79, -82.02) * mm, "end": v(60.62, -80.5) * mm});
            skLineSegment(sketch, "E10.31.6", {"start": v(61.19, -83.5) * mm, "end": v(61.58, -84.6) * mm});
            skArc(sketch, "E10.31.7", {"start": v(61.58, -84.6) * mm, "mid": v(61.9, -86) * mm, "end": v(61.9, -87.45) * mm});
            skArc(sketch, "E10.32.0", {"start": v(78.56, -69.12) * mm, "mid": v(79.93, -69.58) * mm, "end": v(81.37, -69.71) * mm});
            skLineSegment(sketch, "E10.32.1", {"start": v(77.5, -68.63) * mm, "end": v(78.56, -69.12) * mm});
            skArc(sketch, "E10.32.2", {"start": v(77.5, -68.63) * mm, "mid": v(76.06, -68.1) * mm, "end": v(74.56, -67.78) * mm});
            skArc(sketch, "E10.32.3", {"start": v(74.56, -67.78) * mm, "mid": v(72.7, -67.96) * mm, "end": v(71.12, -68.97) * mm});
            skArc(sketch, "E10.32.4", {"start": v(70.05, -72.44) * mm, "mid": v(70.17, -70.57) * mm, "end": v(71.12, -68.97) * mm});
            skArc(sketch, "E10.32.5", {"start": v(70.98, -75.34) * mm, "mid": v(70.4, -73.93) * mm, "end": v(70.05, -72.44) * mm});
            skLineSegment(sketch, "E10.32.6", {"start": v(70.98, -75.34) * mm, "end": v(71.5, -76.4) * mm});
            skArc(sketch, "E10.32.7", {"start": v(71.5, -76.4) * mm, "mid": v(72, -77.75) * mm, "end": v(72.18, -79.18) * mm});
            skArc(sketch, "E10.33.0", {"start": v(86.46, -58.94) * mm, "mid": v(87.87, -59.23) * mm, "end": v(89.32, -59.18) * mm});
            skLineSegment(sketch, "E10.33.1", {"start": v(85.34, -58.59) * mm, "end": v(86.46, -58.94) * mm});
            skArc(sketch, "E10.33.2", {"start": v(85.34, -58.59) * mm, "mid": v(83.85, -58.24) * mm, "end": v(82.33, -58.1) * mm});
            skArc(sketch, "E10.33.3", {"start": v(82.33, -58.1) * mm, "mid": v(80.5, -58.51) * mm, "end": v(79.06, -59.7) * mm});
            skArc(sketch, "E10.33.4", {"start": v(78.42, -63.28) * mm, "mid": v(78.31, -61.42) * mm, "end": v(79.06, -59.7) * mm});
            skArc(sketch, "E10.33.5", {"start": v(79.7, -66.05) * mm, "mid": v(78.96, -64.71) * mm, "end": v(78.42, -63.28) * mm});
            skLineSegment(sketch, "E10.33.6", {"start": v(79.7, -66.05) * mm, "end": v(80.35, -67.02) * mm});
            skArc(sketch, "E10.33.7", {"start": v(80.35, -67.02) * mm, "mid": v(81.01, -68.31) * mm, "end": v(81.37, -69.71) * mm});
            skArc(sketch, "E10.34.0", {"start": v(93.04, -47.87) * mm, "mid": v(94.49, -47.98) * mm, "end": v(95.91, -47.76) * mm});
            skLineSegment(sketch, "E10.34.1", {"start": v(91.9, -47.65) * mm, "end": v(93.04, -47.87) * mm});
            skArc(sketch, "E10.34.2", {"start": v(91.9, -47.65) * mm, "mid": v(90.37, -47.49) * mm, "end": v(88.84, -47.55) * mm});
            skArc(sketch, "E10.34.3", {"start": v(88.84, -47.55) * mm, "mid": v(87.08, -48.18) * mm, "end": v(85.8, -49.53) * mm});
            skArc(sketch, "E10.34.4", {"start": v(85.6, -53.16) * mm, "mid": v(85.26, -51.33) * mm, "end": v(85.8, -49.53) * mm});
            skArc(sketch, "E10.34.5", {"start": v(87.22, -55.75) * mm, "mid": v(86.31, -54.52) * mm, "end": v(85.6, -53.16) * mm});
            skLineSegment(sketch, "E10.34.6", {"start": v(87.22, -55.75) * mm, "end": v(87.98, -56.64) * mm});
            skArc(sketch, "E10.34.7", {"start": v(87.98, -56.64) * mm, "mid": v(88.8, -57.84) * mm, "end": v(89.32, -59.18) * mm});
            skArc(sketch, "E10.35.0", {"start": v(98.22, -36.08) * mm, "mid": v(99.67, -36) * mm, "end": v(101.06, -35.61) * mm});
            skLineSegment(sketch, "E10.35.1", {"start": v(97.05, -36) * mm, "end": v(98.22, -36.08) * mm});
            skArc(sketch, "E10.35.2", {"start": v(97.05, -36) * mm, "mid": v(95.52, -36.02) * mm, "end": v(94.01, -36.27) * mm});
            skArc(sketch, "E10.35.3", {"start": v(94.01, -36.27) * mm, "mid": v(92.34, -37.11) * mm, "end": v(91.23, -38.62) * mm});
            skArc(sketch, "E10.35.4", {"start": v(91.49, -42.24) * mm, "mid": v(90.93, -40.46) * mm, "end": v(91.23, -38.62) * mm});
            skArc(sketch, "E10.35.5", {"start": v(93.4, -44.61) * mm, "mid": v(92.36, -43.5) * mm, "end": v(91.49, -42.24) * mm});
            skLineSegment(sketch, "E10.35.6", {"start": v(93.4, -44.61) * mm, "end": v(94.27, -45.4) * mm});
            skArc(sketch, "E10.35.7", {"start": v(94.27, -45.4) * mm, "mid": v(95.23, -46.49) * mm, "end": v(95.91, -47.76) * mm});
            skArc(sketch, "E10.36.0", {"start": v(101.9, -23.73) * mm, "mid": v(103.33, -23.48) * mm, "end": v(104.67, -22.92) * mm});
            skLineSegment(sketch, "E10.36.1", {"start": v(100.74, -23.8) * mm, "end": v(101.9, -23.73) * mm});
            skArc(sketch, "E10.36.2", {"start": v(100.74, -23.8) * mm, "mid": v(99.22, -24.01) * mm, "end": v(97.76, -24.44) * mm});
            skArc(sketch, "E10.36.3", {"start": v(97.76, -24.44) * mm, "mid": v(96.2, -25.48) * mm, "end": v(95.29, -27.11) * mm});
            skArc(sketch, "E10.36.4", {"start": v(95.98, -30.68) * mm, "mid": v(95.2, -28.98) * mm, "end": v(95.29, -27.11) * mm});
            skArc(sketch, "E10.36.5", {"start": v(98.18, -32.8) * mm, "mid": v(97, -31.82) * mm, "end": v(95.98, -30.68) * mm});
            skLineSegment(sketch, "E10.36.6", {"start": v(98.18, -32.8) * mm, "end": v(99.14, -33.47) * mm});
            skArc(sketch, "E10.36.7", {"start": v(99.14, -33.47) * mm, "mid": v(100.22, -34.43) * mm, "end": v(101.06, -35.61) * mm});
            skArc(sketch, "E10.37.0", {"start": v(104.05, -11.03) * mm, "mid": v(105.44, -10.6) * mm, "end": v(106.7, -9.89) * mm});
            skLineSegment(sketch, "E10.37.1", {"start": v(102.9, -11.24) * mm, "end": v(104.05, -11.03) * mm});
            skArc(sketch, "E10.37.2", {"start": v(102.9, -11.24) * mm, "mid": v(101.42, -11.64) * mm, "end": v(100.02, -12.25) * mm});
            skArc(sketch, "E10.37.3", {"start": v(100.02, -12.25) * mm, "mid": v(98.6, -13.47) * mm, "end": v(97.9, -15.2) * mm});
            skArc(sketch, "E10.37.4", {"start": v(99.03, -18.65) * mm, "mid": v(98.05, -17.06) * mm, "end": v(97.9, -15.2) * mm});
            skArc(sketch, "E10.37.5", {"start": v(101.47, -20.48) * mm, "mid": v(100.18, -19.66) * mm, "end": v(99.03, -18.65) * mm});
            skLineSegment(sketch, "E10.37.6", {"start": v(101.47, -20.48) * mm, "end": v(102.5, -21.03) * mm});
            skArc(sketch, "E10.37.7", {"start": v(102.5, -21.03) * mm, "mid": v(103.7, -21.86) * mm, "end": v(104.67, -22.92) * mm});
            skArc(sketch, "E10.38.0", {"start": v(104.62, 1.84) * mm, "mid": v(105.94, 2.43) * mm, "end": v(107.1, 3.3) * mm});
            skLineSegment(sketch, "E10.38.1", {"start": v(103.5, 1.5) * mm, "end": v(104.62, 1.84) * mm});
            skArc(sketch, "E10.38.2", {"start": v(103.5, 1.5) * mm, "mid": v(102.08, 0.92) * mm, "end": v(100.77, 0.14) * mm});
            skArc(sketch, "E10.38.3", {"start": v(100.77, 0.14) * mm, "mid": v(99.51, -1.25) * mm, "end": v(99.02, -3.05) * mm});
            skArc(sketch, "E10.38.4", {"start": v(100.57, -6.34) * mm, "mid": v(99.4, -4.88) * mm, "end": v(99.02, -3.05) * mm});
            skArc(sketch, "E10.38.5", {"start": v(103.22, -7.86) * mm, "mid": v(101.84, -7.2) * mm, "end": v(100.57, -6.34) * mm});
            skLineSegment(sketch, "E10.38.6", {"start": v(103.22, -7.86) * mm, "end": v(104.3, -8.28) * mm});
            skArc(sketch, "E10.38.7", {"start": v(104.3, -8.28) * mm, "mid": v(105.6, -8.95) * mm, "end": v(106.7, -9.89) * mm});
            skArc(sketch, "E10.39.0", {"start": v(103.6, 14.69) * mm, "mid": v(104.84, 15.43) * mm, "end": v(105.88, 16.44) * mm});
            skLineSegment(sketch, "E10.39.1", {"start": v(102.54, 14.2) * mm, "end": v(103.6, 14.69) * mm});
            skArc(sketch, "E10.39.2", {"start": v(102.54, 14.2) * mm, "mid": v(101.2, 13.45) * mm, "end": v(99.99, 12.52) * mm});
            skArc(sketch, "E10.39.3", {"start": v(99.99, 12.52) * mm, "mid": v(98.91, 11) * mm, "end": v(98.65, 9.14) * mm});
            skArc(sketch, "E10.39.4", {"start": v(100.58, 6.07) * mm, "mid": v(99.25, 7.37) * mm, "end": v(98.65, 9.14) * mm});
            skArc(sketch, "E10.39.5", {"start": v(103.4, 4.88) * mm, "mid": v(101.95, 5.37) * mm, "end": v(100.58, 6.07) * mm});
            skLineSegment(sketch, "E10.39.6", {"start": v(103.4, 4.88) * mm, "end": v(104.54, 4.6) * mm});
            skArc(sketch, "E10.39.7", {"start": v(104.54, 4.6) * mm, "mid": v(105.89, 4.1) * mm, "end": v(107.1, 3.3) * mm});
            skArc(sketch, "E10.40.0", {"start": v(101.01, 27.3) * mm, "mid": v(102.15, 28.2) * mm, "end": v(103.06, 29.32) * mm});
            skLineSegment(sketch, "E10.40.1", {"start": v(100.01, 26.7) * mm, "end": v(101.01, 27.3) * mm});
            skArc(sketch, "E10.40.2", {"start": v(100.01, 26.7) * mm, "mid": v(98.78, 25.79) * mm, "end": v(97.69, 24.71) * mm});
            skArc(sketch, "E10.40.3", {"start": v(97.69, 24.71) * mm, "mid": v(96.81, 23.06) * mm, "end": v(96.78, 21.2) * mm});
            skArc(sketch, "E10.40.4", {"start": v(99.08, 18.38) * mm, "mid": v(97.59, 19.51) * mm, "end": v(96.78, 21.2) * mm});
            skArc(sketch, "E10.40.5", {"start": v(102.01, 17.55) * mm, "mid": v(100.51, 17.86) * mm, "end": v(99.08, 18.38) * mm});
            skLineSegment(sketch, "E10.40.6", {"start": v(102.01, 17.55) * mm, "end": v(103.18, 17.41) * mm});
            skArc(sketch, "E10.40.7", {"start": v(103.18, 17.41) * mm, "mid": v(104.58, 17.08) * mm, "end": v(105.88, 16.44) * mm});
            skArc(sketch, "E10.41.0", {"start": v(96.89, 39.51) * mm, "mid": v(97.9, 40.54) * mm, "end": v(98.67, 41.76) * mm});
            skLineSegment(sketch, "E10.41.1", {"start": v(95.98, 38.78) * mm, "end": v(96.89, 39.51) * mm});
            skArc(sketch, "E10.41.2", {"start": v(95.98, 38.78) * mm, "mid": v(94.86, 37.73) * mm, "end": v(93.91, 36.53) * mm});
            skArc(sketch, "E10.41.3", {"start": v(93.91, 36.53) * mm, "mid": v(93.24, 34.78) * mm, "end": v(93.44, 32.93) * mm});
            skArc(sketch, "E10.41.4", {"start": v(96.07, 30.42) * mm, "mid": v(94.45, 31.36) * mm, "end": v(93.44, 32.93) * mm});
            skArc(sketch, "E10.41.5", {"start": v(99.08, 29.96) * mm, "mid": v(97.56, 30.08) * mm, "end": v(96.07, 30.42) * mm});
            skLineSegment(sketch, "E10.41.6", {"start": v(99.08, 29.96) * mm, "end": v(100.26, 29.96) * mm});
            skArc(sketch, "E10.41.7", {"start": v(100.26, 29.96) * mm, "mid": v(101.7, 29.8) * mm, "end": v(103.06, 29.32) * mm});
            skArc(sketch, "E10.42.0", {"start": v(91.3, 51.12) * mm, "mid": v(92.19, 52.26) * mm, "end": v(92.8, 53.57) * mm});
            skLineSegment(sketch, "E10.42.1", {"start": v(90.48, 50.28) * mm, "end": v(91.3, 51.12) * mm});
            skArc(sketch, "E10.42.2", {"start": v(90.48, 50.28) * mm, "mid": v(89.5, 49.1) * mm, "end": v(88.71, 47.8) * mm});
            skArc(sketch, "E10.42.3", {"start": v(88.71, 47.8) * mm, "mid": v(88.26, 45.98) * mm, "end": v(88.68, 44.16) * mm});
            skArc(sketch, "E10.42.4", {"start": v(91.6, 42) * mm, "mid": v(89.88, 42.73) * mm, "end": v(88.68, 44.16) * mm});
            skArc(sketch, "E10.42.5", {"start": v(94.65, 41.9) * mm, "mid": v(93.12, 41.84) * mm, "end": v(91.6, 42) * mm});
            skLineSegment(sketch, "E10.42.6", {"start": v(94.65, 41.9) * mm, "end": v(95.81, 42.05) * mm});
            skArc(sketch, "E10.42.7", {"start": v(95.81, 42.05) * mm, "mid": v(97.26, 42.07) * mm, "end": v(98.67, 41.76) * mm});
            skArc(sketch, "E10.43.0", {"start": v(84.33, 61.95) * mm, "mid": v(85.06, 63.2) * mm, "end": v(85.5, 64.57) * mm});
            skLineSegment(sketch, "E10.43.1", {"start": v(83.62, 61.02) * mm, "end": v(84.33, 61.95) * mm});
            skArc(sketch, "E10.43.2", {"start": v(83.62, 61.02) * mm, "mid": v(82.8, 59.73) * mm, "end": v(82.17, 58.33) * mm});
            skArc(sketch, "E10.43.3", {"start": v(82.17, 58.33) * mm, "mid": v(81.94, 56.48) * mm, "end": v(82.58, 54.72) * mm});
            skArc(sketch, "E10.43.4", {"start": v(85.75, 52.93) * mm, "mid": v(83.95, 53.45) * mm, "end": v(82.58, 54.72) * mm});
            skArc(sketch, "E10.43.5", {"start": v(88.78, 53.22) * mm, "mid": v(87.28, 52.96) * mm, "end": v(85.75, 52.93) * mm});
            skLineSegment(sketch, "E10.43.6", {"start": v(88.78, 53.22) * mm, "end": v(89.92, 53.5) * mm});
            skArc(sketch, "E10.43.7", {"start": v(89.92, 53.5) * mm, "mid": v(91.35, 53.7) * mm, "end": v(92.8, 53.57) * mm});
            skArc(sketch, "E10.44.0", {"start": v(76.07, 71.84) * mm, "mid": v(76.65, 73.17) * mm, "end": v(76.92, 74.59) * mm});
            skLineSegment(sketch, "E10.44.1", {"start": v(75.49, 70.83) * mm, "end": v(76.07, 71.84) * mm});
            skArc(sketch, "E10.44.2", {"start": v(75.49, 70.83) * mm, "mid": v(74.83, 69.45) * mm, "end": v(74.37, 67.99) * mm});
            skArc(sketch, "E10.44.3", {"start": v(74.37, 67.99) * mm, "mid": v(74.38, 66.12) * mm, "end": v(75.23, 64.46) * mm});
            skArc(sketch, "E10.44.4", {"start": v(78.6, 63.07) * mm, "mid": v(76.75, 63.36) * mm, "end": v(75.23, 64.46) * mm});
            skArc(sketch, "E10.44.5", {"start": v(81.57, 63.73) * mm, "mid": v(80.1, 63.29) * mm, "end": v(78.6, 63.07) * mm});
            skLineSegment(sketch, "E10.44.6", {"start": v(81.57, 63.73) * mm, "end": v(82.66, 64.15) * mm});
            skArc(sketch, "E10.44.7", {"start": v(82.66, 64.15) * mm, "mid": v(84.06, 64.52) * mm, "end": v(85.5, 64.57) * mm});
            skArc(sketch, "E10.45.0", {"start": v(66.67, 80.65) * mm, "mid": v(67.08, 82.03) * mm, "end": v(67.17, 83.48) * mm});
            skLineSegment(sketch, "E10.45.1", {"start": v(66.2, 79.57) * mm, "end": v(66.67, 80.65) * mm});
            skArc(sketch, "E10.45.2", {"start": v(66.2, 79.57) * mm, "mid": v(65.72, 78.12) * mm, "end": v(65.46, 76.61) * mm});
            skArc(sketch, "E10.45.3", {"start": v(65.46, 76.61) * mm, "mid": v(65.7, 74.76) * mm, "end": v(66.74, 73.21) * mm});
            skArc(sketch, "E10.45.4", {"start": v(70.25, 72.25) * mm, "mid": v(68.38, 72.31) * mm, "end": v(66.74, 73.21) * mm});
            skArc(sketch, "E10.45.5", {"start": v(73.12, 73.27) * mm, "mid": v(71.72, 72.65) * mm, "end": v(70.25, 72.25) * mm});
            skLineSegment(sketch, "E10.45.6", {"start": v(73.12, 73.27) * mm, "end": v(74.15, 73.83) * mm});
            skArc(sketch, "E10.45.7", {"start": v(74.15, 73.83) * mm, "mid": v(75.5, 74.36) * mm, "end": v(76.92, 74.59) * mm});
            skArc(sketch, "E10.46.0", {"start": v(56.25, 88.23) * mm, "mid": v(56.5, 89.66) * mm, "end": v(56.4, 91.1) * mm});
            skLineSegment(sketch, "E10.46.1", {"start": v(55.93, 87.1) * mm, "end": v(56.25, 88.23) * mm});
            skArc(sketch, "E10.46.2", {"start": v(55.93, 87.1) * mm, "mid": v(55.63, 85.6) * mm, "end": v(55.54, 84.08) * mm});
            skArc(sketch, "E10.46.3", {"start": v(55.54, 84.08) * mm, "mid": v(56, 82.27) * mm, "end": v(57.24, 80.86) * mm});
            skArc(sketch, "E10.46.4", {"start": v(60.84, 80.33) * mm, "mid": v(58.97, 80.17) * mm, "end": v(57.24, 80.86) * mm});
            skArc(sketch, "E10.46.5", {"start": v(63.56, 81.7) * mm, "mid": v(62.25, 80.91) * mm, "end": v(60.84, 80.33) * mm});
            skLineSegment(sketch, "E10.46.6", {"start": v(63.56, 81.7) * mm, "end": v(64.52, 82.38) * mm});
            skArc(sketch, "E10.46.7", {"start": v(64.52, 82.38) * mm, "mid": v(65.78, 83.08) * mm, "end": v(67.17, 83.48) * mm});
            skArc(sketch, "E10.47.0", {"start": v(44.98, 94.47) * mm, "mid": v(45.05, 95.92) * mm, "end": v(44.78, 97.34) * mm});
            skLineSegment(sketch, "E10.47.1", {"start": v(44.8, 93.32) * mm, "end": v(44.98, 94.47) * mm});
            skArc(sketch, "E10.47.2", {"start": v(44.8, 93.32) * mm, "mid": v(44.68, 91.8) * mm, "end": v(44.8, 90.26) * mm});
            skArc(sketch, "E10.47.3", {"start": v(44.8, 90.26) * mm, "mid": v(45.47, 88.52) * mm, "end": v(46.87, 87.28) * mm});
            skArc(sketch, "E10.47.4", {"start": v(50.5, 87.2) * mm, "mid": v(48.68, 86.8) * mm, "end": v(46.87, 87.28) * mm});
            skArc(sketch, "E10.47.5", {"start": v(53.04, 88.9) * mm, "mid": v(51.83, 87.95) * mm, "end": v(50.5, 87.2) * mm});
            skLineSegment(sketch, "E10.47.6", {"start": v(53.04, 88.9) * mm, "end": v(53.9, 89.68) * mm});
            skArc(sketch, "E10.47.7", {"start": v(53.9, 89.68) * mm, "mid": v(55.08, 90.53) * mm, "end": v(56.4, 91.1) * mm});
            skArc(sketch, "E10.48.0", {"start": v(33.03, 99.29) * mm, "mid": v(32.92, 100.73) * mm, "end": v(32.48, 102.1) * mm});
            skLineSegment(sketch, "E10.48.1", {"start": v(33, 98.11) * mm, "end": v(33.03, 99.29) * mm});
            skArc(sketch, "E10.48.2", {"start": v(33, 98.11) * mm, "mid": v(33.07, 96.59) * mm, "end": v(33.36, 95.08) * mm});
            skArc(sketch, "E10.48.3", {"start": v(33.36, 95.08) * mm, "mid": v(34.25, 93.44) * mm, "end": v(35.79, 92.38) * mm});
            skArc(sketch, "E10.48.4", {"start": v(39.4, 92.74) * mm, "mid": v(37.64, 92.13) * mm, "end": v(35.79, 92.38) * mm});
            skArc(sketch, "E10.48.5", {"start": v(41.72, 94.74) * mm, "mid": v(40.63, 93.65) * mm, "end": v(39.4, 92.74) * mm});
            skLineSegment(sketch, "E10.48.6", {"start": v(41.72, 94.74) * mm, "end": v(42.48, 95.63) * mm});
            skArc(sketch, "E10.48.7", {"start": v(42.48, 95.63) * mm, "mid": v(43.53, 96.61) * mm, "end": v(44.78, 97.34) * mm});
            skArc(sketch, "E10.49.0", {"start": v(20.58, 102.6) * mm, "mid": v(20.3, 104) * mm, "end": v(19.69, 105.32) * mm});
            skLineSegment(sketch, "E10.49.1", {"start": v(20.69, 101.43) * mm, "end": v(20.58, 102.6) * mm});
            skArc(sketch, "E10.49.2", {"start": v(20.69, 101.43) * mm, "mid": v(20.95, 99.92) * mm, "end": v(21.42, 98.46) * mm});
            skArc(sketch, "E10.49.3", {"start": v(21.42, 98.46) * mm, "mid": v(22.5, 96.94) * mm, "end": v(24.16, 96.08) * mm});
            skArc(sketch, "E10.49.4", {"start": v(27.7, 96.88) * mm, "mid": v(26.03, 96.06) * mm, "end": v(24.16, 96.08) * mm});
            skArc(sketch, "E10.49.5", {"start": v(29.76, 99.14) * mm, "mid": v(28.82, 97.94) * mm, "end": v(27.7, 96.88) * mm});
            skLineSegment(sketch, "E10.49.6", {"start": v(29.76, 99.14) * mm, "end": v(30.4, 100.12) * mm});
            skArc(sketch, "E10.49.7", {"start": v(30.4, 100.12) * mm, "mid": v(31.33, 101.23) * mm, "end": v(32.48, 102.1) * mm});
            skArc(sketch, "E10.50.0", {"start": v(7.82, 104.34) * mm, "mid": v(7.36, 105.71) * mm, "end": v(6.6, 106.94) * mm});
            skLineSegment(sketch, "E10.50.1", {"start": v(8.07, 103.2) * mm, "end": v(7.82, 104.34) * mm});
            skArc(sketch, "E10.50.2", {"start": v(8.07, 103.2) * mm, "mid": v(8.5, 101.73) * mm, "end": v(9.16, 100.35) * mm});
            skArc(sketch, "E10.50.3", {"start": v(9.16, 100.35) * mm, "mid": v(10.42, 98.97) * mm, "end": v(12.17, 98.32) * mm});
            skArc(sketch, "E10.50.4", {"start": v(15.6, 99.55) * mm, "mid": v(14.03, 98.53) * mm, "end": v(12.17, 98.32) * mm});
            skArc(sketch, "E10.50.5", {"start": v(17.35, 102.05) * mm, "mid": v(16.56, 100.74) * mm, "end": v(15.6, 99.55) * mm});
            skLineSegment(sketch, "E10.50.6", {"start": v(17.35, 102.05) * mm, "end": v(17.87, 103.1) * mm});
            skArc(sketch, "E10.50.7", {"start": v(17.87, 103.1) * mm, "mid": v(18.65, 104.31) * mm, "end": v(19.69, 105.32) * mm});
            skCircle(sketch, "E11", {"center": v(0, 0) * mm, "radius": 105.37 * mm});
            skCircle(sketch, "E12", {"center": v(0, 0) * mm, "radius": 96.57 * mm});
            skCircle(sketch, "E13", {"center": v(0, 0) * mm, "radius": 65 * mm});
            skCircle(sketch, "E14", {"center": v(0, -65) * mm, "radius": 5 * mm});
            skCircle(sketch, "E15", {"center": v(0, 72) * mm, "radius": 5 * mm});
            skCircle(sketch, "E16.1.0", {"center": v(-68.48, 22.25) * mm, "radius": 5 * mm});
            skCircle(sketch, "E16.2.0", {"center": v(-42.32, -58.25) * mm, "radius": 5 * mm});
            skCircle(sketch, "E16.3.0", {"center": v(42.32, -58.25) * mm, "radius": 5 * mm});
            skCircle(sketch, "E16.4.0", {"center": v(68.48, 22.25) * mm, "radius": 5 * mm});
            skSolve(sketch);
        }
        {
            var Q0;
            Q0=makeQuery(id+"F0.imprint","IMPRINT",FACE,{"disambiguationData":[TD([[makeQuery(id+"F0.imprint","IMPRINT",EDGE,{"derivedFrom":sQuery(id+"F0.wireOp",EDGE,"E12")}),1.0]])]});
            extrude(context, id + "F1", {"entities" : qUnion([Q0]), "endBound" : BoundingType.SYMMETRIC, "depth" : 4.5 * mm});
        }
        {
            var Q0;
            Q0=makeQuery(id+"F0.imprint","IMPRINT",FACE,{"disambiguationData":[TD([[makeQuery(id+"F0.imprint","IMPRINT",EDGE,{"derivedFrom":sQuery(id+"F0.wireOp",EDGE,"E1")}),-1.0]])]});
            extrude(context, id + "F2", {"entities" : qUnion([Q0]), "operationType" : NewBodyOperationType.ADD, "endBound" : BoundingType.SYMMETRIC, "depth" : 3.5 * mm});
        }
        {
            var Q0;
            {var subQ0=sQuery(id+"F0.wireOp",EDGE,"E14");var subQ1=sQuery(id+"F0.wireOp",EDGE,"E13");Q0=makeQuery(id+"F1.opExtrude","SWEPT_EDGE",EDGE,{"disambiguationData":[OSD([subQ1,subQ0]),TDD([makeQuery(id+"F0.imprint","INTERSECT",VERTEX,{"disambiguationData":[OD(1.0)],"derivedFrom":[subQ1,subQ0]})])]});}
            var Q1;
            {var subQ0=sQuery(id+"F0.wireOp",EDGE,"E14");var subQ1=sQuery(id+"F0.wireOp",EDGE,"E13");Q1=makeQuery(id+"F1.opExtrude","SWEPT_EDGE",EDGE,{"disambiguationData":[OSD([subQ1,subQ0]),TDD([makeQuery(id+"F0.imprint","INTERSECT",VERTEX,{"disambiguationData":[OD(0.0)],"derivedFrom":[subQ1,subQ0]})])]});}
            fillet(context, id + "F3", {"entities" : qUnion([Q0, Q1]), "radius" : 5.08 * mm, "tangentPropagation" : true, "allowEdgeOverflow" : false});
        }
        {
            var Q0;
            Q0=makeQuery(id+"F1.opExtrude","CAP_FACE",FACE,{"disambiguationData":[OSD([sQuery(id+"F0.wireOp",EDGE,"E12"),sQuery(id+"F0.wireOp",EDGE,"E13"),sQuery(id+"F0.wireOp",EDGE,"E14"),sQuery(id+"F0.wireOp",EDGE,"E15"),sQuery(id+"F0.wireOp",EDGE,"E16.1.0"),sQuery(id+"F0.wireOp",EDGE,"E16.2.0"),sQuery(id+"F0.wireOp",EDGE,"E16.3.0"),sQuery(id+"F0.wireOp",EDGE,"E16.4.0")])],"isStart":false});
            var sketch = newSketch(context, id + "F4", { "sketchPlane" : qUnion([Q0])});
            skArc(sketch, "E17", {"start": v(63.6, -65.76) * mm, "mid": v(68.08, -61.12) * mm, "end": v(72.2, -56.18) * mm});
            skArc(sketch, "E18", {"start": v(48.72, -50.37) * mm, "mid": v(52.15, -46.82) * mm, "end": v(55.31, -43.03) * mm});
            skLineSegment(sketch, "E19", {"start": v(48.72, -50.37) * mm, "end": v(63.6, -65.76) * mm});
            skLineSegment(sketch, "E20", {"start": v(69.03, 12.11) * mm, "end": v(90.11, 15.81) * mm});
            skLineSegment(sketch, "E21", {"start": v(70.04, 2.3) * mm, "end": v(91.44, 3) * mm});
            skLineSegment(sketch, "E22", {"start": v(70.08, 0.47) * mm, "end": v(91.49, 0.61) * mm});
            skLineSegment(sketch, "E23", {"start": v(69.45, -9.37) * mm, "end": v(90.67, -12.23) * mm});
            skLineSegment(sketch, "E24", {"start": v(69.18, -11.18) * mm, "end": v(90.32, -14.6) * mm});
            skLineSegment(sketch, "E25", {"start": v(66.93, -20.78) * mm, "end": v(87.37, -27.13) * mm});
            skLineSegment(sketch, "E26", {"start": v(66.36, -22.53) * mm, "end": v(86.63, -29.4) * mm});
            skLineSegment(sketch, "E27", {"start": v(62.54, -31.62) * mm, "end": v(81.65, -41.28) * mm});
            skLineSegment(sketch, "E28", {"start": v(61.7, -33.24) * mm, "end": v(80.54, -43.4) * mm});
            skLineSegment(sketch, "E29", {"start": v(56.42, -41.57) * mm, "end": v(73.65, -54.27) * mm});
            skLineSegment(sketch, "E30", {"start": v(55.31, -43.03) * mm, "end": v(72.2, -56.18) * mm});
            skArc(sketch, "E31.trimOffspring", {"start": v(56.42, -41.57) * mm, "mid": v(59.2, -37.5) * mm, "end": v(61.7, -33.24) * mm});
            skArc(sketch, "E32.trimOffspring", {"start": v(73.65, -54.27) * mm, "mid": v(77.29, -48.96) * mm, "end": v(80.54, -43.4) * mm});
            skArc(sketch, "E33.trimOffspring", {"start": v(81.65, -41.28) * mm, "mid": v(84.35, -35.43) * mm, "end": v(86.63, -29.4) * mm});
            skArc(sketch, "E34.trimOffspring", {"start": v(62.54, -31.62) * mm, "mid": v(64.61, -27.14) * mm, "end": v(66.36, -22.53) * mm});
            skArc(sketch, "E35.trimOffspring", {"start": v(87.37, -27.13) * mm, "mid": v(89.07, -20.92) * mm, "end": v(90.32, -14.6) * mm});
            skArc(sketch, "E36.trimOffspring", {"start": v(66.93, -20.78) * mm, "mid": v(68.22, -16.02) * mm, "end": v(69.18, -11.18) * mm});
            skArc(sketch, "E37.trimOffspring", {"start": v(69.45, -9.37) * mm, "mid": v(69.94, -4.46) * mm, "end": v(70.08, 0.47) * mm});
            skArc(sketch, "E38.trimOffspring", {"start": v(70.04, 2.3) * mm, "mid": v(69.7, 7.23) * mm, "end": v(69.03, 12.11) * mm});
            skArc(sketch, "E39.trimOffspring", {"start": v(91.44, 3) * mm, "mid": v(91, 9.43) * mm, "end": v(90.11, 15.81) * mm});
            skArc(sketch, "E40.trimOffspring", {"start": v(90.67, -12.23) * mm, "mid": v(91.3, -5.82) * mm, "end": v(91.49, 0.61) * mm});
            skArc(sketch, "E41.1.0", {"start": v(62.96, 30.77) * mm, "mid": v(60.64, 35.13) * mm, "end": v(58.02, 39.3) * mm});
            skLineSegment(sketch, "E41.1.1", {"start": v(50.68, 48.4) * mm, "end": v(66.16, 63.19) * mm});
            skArc(sketch, "E41.1.2", {"start": v(52.8, 74.71) * mm, "mid": v(47.42, 78.24) * mm, "end": v(41.8, 81.38) * mm});
            skLineSegment(sketch, "E41.1.3", {"start": v(9.81, 69.39) * mm, "end": v(12.8, 90.59) * mm});
            skLineSegment(sketch, "E41.1.4", {"start": v(58.02, 39.3) * mm, "end": v(75.75, 51.31) * mm});
            skArc(sketch, "E41.1.5", {"start": v(56.97, 40.81) * mm, "mid": v(53.96, 44.72) * mm, "end": v(50.68, 48.4) * mm});
            skLineSegment(sketch, "E41.1.6", {"start": v(19.45, 67.33) * mm, "end": v(25.4, 87.9) * mm});
            skLineSegment(sketch, "E41.1.7", {"start": v(21.2, 66.8) * mm, "end": v(27.69, 87.2) * mm});
            skLineSegment(sketch, "E41.1.8", {"start": v(62.96, 30.77) * mm, "end": v(82.2, 40.18) * mm});
            skArc(sketch, "E41.1.9", {"start": v(40.45, 57.23) * mm, "mid": v(36.32, 59.93) * mm, "end": v(32.01, 62.34) * mm});
            skArc(sketch, "E41.1.10", {"start": v(82.2, 40.18) * mm, "mid": v(79.17, 45.86) * mm, "end": v(75.75, 51.31) * mm});
            skArc(sketch, "E41.1.11", {"start": v(74.38, 53.28) * mm, "mid": v(70.44, 58.38) * mm, "end": v(66.16, 63.19) * mm});
            skArc(sketch, "E41.1.12", {"start": v(30.37, 63.16) * mm, "mid": v(25.85, 65.14) * mm, "end": v(21.2, 66.8) * mm});
            skArc(sketch, "E41.1.13", {"start": v(64.49, 64.9) * mm, "mid": v(59.76, 69.27) * mm, "end": v(54.74, 73.3) * mm});
            skArc(sketch, "E41.1.14", {"start": v(39.65, 82.45) * mm, "mid": v(33.75, 85.04) * mm, "end": v(27.69, 87.2) * mm});
            skLineSegment(sketch, "E41.1.15", {"start": v(41.93, 56.15) * mm, "end": v(54.74, 73.3) * mm});
            skLineSegment(sketch, "E41.1.16", {"start": v(30.37, 63.16) * mm, "end": v(39.65, 82.45) * mm});
            skLineSegment(sketch, "E41.1.17", {"start": v(40.45, 57.23) * mm, "end": v(52.8, 74.71) * mm});
            skLineSegment(sketch, "E41.1.18", {"start": v(49.4, 49.71) * mm, "end": v(64.49, 64.9) * mm});
            skLineSegment(sketch, "E41.1.19", {"start": v(32.01, 62.34) * mm, "end": v(41.8, 81.38) * mm});
            skArc(sketch, "E41.1.20", {"start": v(25.4, 87.9) * mm, "mid": v(19.15, 89.46) * mm, "end": v(12.8, 90.59) * mm});
            skLineSegment(sketch, "E41.1.21", {"start": v(56.97, 40.81) * mm, "end": v(74.38, 53.28) * mm});
            skArc(sketch, "E41.1.22", {"start": v(19.45, 67.33) * mm, "mid": v(14.67, 68.53) * mm, "end": v(9.81, 69.39) * mm});
            skArc(sketch, "E41.1.23", {"start": v(49.4, 49.71) * mm, "mid": v(45.78, 53.06) * mm, "end": v(41.93, 56.15) * mm});
            skArc(sketch, "E41.2.0", {"start": v(-9.81, 69.39) * mm, "mid": v(-14.67, 68.53) * mm, "end": v(-19.45, 67.33) * mm});
            skLineSegment(sketch, "E41.2.1", {"start": v(-30.37, 63.16) * mm, "end": v(-39.65, 82.45) * mm});
            skArc(sketch, "E41.2.2", {"start": v(-54.74, 73.3) * mm, "mid": v(-59.76, 69.27) * mm, "end": v(-64.49, 64.9) * mm});
            skLineSegment(sketch, "E41.2.3", {"start": v(-62.96, 30.77) * mm, "end": v(-82.2, 40.18) * mm});
            skLineSegment(sketch, "E41.2.4", {"start": v(-19.45, 67.33) * mm, "end": v(-25.4, 87.9) * mm});
            skArc(sketch, "E41.2.5", {"start": v(-21.2, 66.8) * mm, "mid": v(-25.85, 65.14) * mm, "end": v(-30.37, 63.16) * mm});
            skLineSegment(sketch, "E41.2.6", {"start": v(-58.02, 39.3) * mm, "end": v(-75.75, 51.31) * mm});
            skLineSegment(sketch, "E41.2.7", {"start": v(-56.97, 40.81) * mm, "end": v(-74.38, 53.28) * mm});
            skLineSegment(sketch, "E41.2.8", {"start": v(-9.81, 69.39) * mm, "end": v(-12.8, 90.59) * mm});
            skArc(sketch, "E41.2.9", {"start": v(-41.93, 56.15) * mm, "mid": v(-45.78, 53.06) * mm, "end": v(-49.4, 49.71) * mm});
            skArc(sketch, "E41.2.10", {"start": v(-12.8, 90.59) * mm, "mid": v(-19.15, 89.46) * mm, "end": v(-25.4, 87.9) * mm});
            skArc(sketch, "E41.2.11", {"start": v(-27.69, 87.2) * mm, "mid": v(-33.75, 85.04) * mm, "end": v(-39.65, 82.45) * mm});
            skArc(sketch, "E41.2.12", {"start": v(-50.68, 48.4) * mm, "mid": v(-53.96, 44.72) * mm, "end": v(-56.97, 40.81) * mm});
            skArc(sketch, "E41.2.13", {"start": v(-41.8, 81.38) * mm, "mid": v(-47.42, 78.24) * mm, "end": v(-52.8, 74.71) * mm});
            skArc(sketch, "E41.2.14", {"start": v(-66.16, 63.19) * mm, "mid": v(-70.44, 58.38) * mm, "end": v(-74.38, 53.28) * mm});
            skLineSegment(sketch, "E41.2.15", {"start": v(-40.45, 57.23) * mm, "end": v(-52.8, 74.71) * mm});
            skLineSegment(sketch, "E41.2.16", {"start": v(-50.68, 48.4) * mm, "end": v(-66.16, 63.19) * mm});
            skLineSegment(sketch, "E41.2.17", {"start": v(-41.93, 56.15) * mm, "end": v(-54.74, 73.3) * mm});
            skLineSegment(sketch, "E41.2.18", {"start": v(-32.01, 62.34) * mm, "end": v(-41.8, 81.38) * mm});
            skLineSegment(sketch, "E41.2.19", {"start": v(-49.4, 49.71) * mm, "end": v(-64.49, 64.9) * mm});
            skArc(sketch, "E41.2.20", {"start": v(-75.75, 51.31) * mm, "mid": v(-79.17, 45.86) * mm, "end": v(-82.2, 40.18) * mm});
            skLineSegment(sketch, "E41.2.21", {"start": v(-21.2, 66.8) * mm, "end": v(-27.69, 87.2) * mm});
            skArc(sketch, "E41.2.22", {"start": v(-58.02, 39.3) * mm, "mid": v(-60.64, 35.13) * mm, "end": v(-62.96, 30.77) * mm});
            skArc(sketch, "E41.2.23", {"start": v(-32.01, 62.34) * mm, "mid": v(-36.32, 59.93) * mm, "end": v(-40.45, 57.23) * mm});
            skArc(sketch, "E41.3.0", {"start": v(-69.03, 12.11) * mm, "mid": v(-69.7, 7.23) * mm, "end": v(-70.04, 2.3) * mm});
            skLineSegment(sketch, "E41.3.1", {"start": v(-69.45, -9.37) * mm, "end": v(-90.67, -12.23) * mm});
            skArc(sketch, "E41.3.2", {"start": v(-86.63, -29.4) * mm, "mid": v(-84.35, -35.43) * mm, "end": v(-81.65, -41.28) * mm});
            skLineSegment(sketch, "E41.3.3", {"start": v(-48.72, -50.37) * mm, "end": v(-63.6, -65.76) * mm});
            skLineSegment(sketch, "E41.3.4", {"start": v(-70.04, 2.3) * mm, "end": v(-91.44, 3) * mm});
            skArc(sketch, "E41.3.5", {"start": v(-70.08, 0.47) * mm, "mid": v(-69.94, -4.46) * mm, "end": v(-69.45, -9.37) * mm});
            skLineSegment(sketch, "E41.3.6", {"start": v(-55.31, -43.03) * mm, "end": v(-72.2, -56.18) * mm});
            skLineSegment(sketch, "E41.3.7", {"start": v(-56.42, -41.57) * mm, "end": v(-73.65, -54.27) * mm});
            skLineSegment(sketch, "E41.3.8", {"start": v(-69.03, 12.11) * mm, "end": v(-90.11, 15.81) * mm});
            skArc(sketch, "E41.3.9", {"start": v(-66.36, -22.53) * mm, "mid": v(-64.61, -27.14) * mm, "end": v(-62.54, -31.62) * mm});
            skArc(sketch, "E41.3.10", {"start": v(-90.11, 15.81) * mm, "mid": v(-91, 9.43) * mm, "end": v(-91.44, 3) * mm});
            skArc(sketch, "E41.3.11", {"start": v(-91.49, 0.61) * mm, "mid": v(-91.3, -5.82) * mm, "end": v(-90.67, -12.23) * mm});
            skArc(sketch, "E41.3.12", {"start": v(-61.7, -33.24) * mm, "mid": v(-59.2, -37.5) * mm, "end": v(-56.42, -41.57) * mm});
            skArc(sketch, "E41.3.13", {"start": v(-90.32, -14.6) * mm, "mid": v(-89.07, -20.92) * mm, "end": v(-87.37, -27.13) * mm});
            skArc(sketch, "E41.3.14", {"start": v(-80.54, -43.4) * mm, "mid": v(-77.29, -48.96) * mm, "end": v(-73.65, -54.27) * mm});
            skLineSegment(sketch, "E41.3.15", {"start": v(-66.93, -20.78) * mm, "end": v(-87.37, -27.13) * mm});
            skLineSegment(sketch, "E41.3.16", {"start": v(-61.7, -33.24) * mm, "end": v(-80.54, -43.4) * mm});
            skLineSegment(sketch, "E41.3.17", {"start": v(-66.36, -22.53) * mm, "end": v(-86.63, -29.4) * mm});
            skLineSegment(sketch, "E41.3.18", {"start": v(-69.18, -11.18) * mm, "end": v(-90.32, -14.6) * mm});
            skLineSegment(sketch, "E41.3.19", {"start": v(-62.54, -31.62) * mm, "end": v(-81.65, -41.28) * mm});
            skArc(sketch, "E41.3.20", {"start": v(-72.2, -56.18) * mm, "mid": v(-68.08, -61.12) * mm, "end": v(-63.6, -65.76) * mm});
            skLineSegment(sketch, "E41.3.21", {"start": v(-70.08, 0.47) * mm, "end": v(-91.49, 0.61) * mm});
            skArc(sketch, "E41.3.22", {"start": v(-55.31, -43.03) * mm, "mid": v(-52.15, -46.82) * mm, "end": v(-48.72, -50.37) * mm});
            skArc(sketch, "E41.3.23", {"start": v(-69.18, -11.18) * mm, "mid": v(-68.22, -16.02) * mm, "end": v(-66.93, -20.78) * mm});
            skSolve(sketch);
        }
        {
            var Q0;
            Q0=makeQuery(id+"F4.imprint","IMPRINT",FACE,{"disambiguationData":[TD([[makeQuery(id+"F4.imprint","IMPRINT",EDGE,{"derivedFrom":sQuery(id+"F4.wireOp",EDGE,"E41.3.3")}),-1.0]])]});
            var Q1;
            Q1=makeQuery(id+"F4.imprint","IMPRINT",FACE,{"disambiguationData":[TD([[makeQuery(id+"F4.imprint","IMPRINT",EDGE,{"derivedFrom":sQuery(id+"F4.wireOp",EDGE,"E41.3.7")}),-1.0]])]});
            var Q2;
            Q2=makeQuery(id+"F4.imprint","IMPRINT",FACE,{"disambiguationData":[TD([[makeQuery(id+"F4.imprint","IMPRINT",EDGE,{"derivedFrom":sQuery(id+"F4.wireOp",EDGE,"E41.3.1")}),-1.0]])]});
            var Q3;
            Q3=makeQuery(id+"F4.imprint","IMPRINT",FACE,{"disambiguationData":[TD([[makeQuery(id+"F4.imprint","IMPRINT",EDGE,{"derivedFrom":sQuery(id+"F4.wireOp",EDGE,"E41.3.0")}),-1.0]])]});
            var Q4;
            Q4=makeQuery(id+"F4.imprint","IMPRINT",FACE,{"disambiguationData":[TD([[makeQuery(id+"F4.imprint","IMPRINT",EDGE,{"derivedFrom":sQuery(id+"F4.wireOp",EDGE,"E41.2.3")}),-1.0]])]});
            var Q5;
            Q5=makeQuery(id+"F4.imprint","IMPRINT",FACE,{"disambiguationData":[TD([[makeQuery(id+"F4.imprint","IMPRINT",EDGE,{"derivedFrom":sQuery(id+"F4.wireOp",EDGE,"E41.2.7")}),-1.0]])]});
            var Q6;
            Q6=makeQuery(id+"F4.imprint","IMPRINT",FACE,{"disambiguationData":[TD([[makeQuery(id+"F4.imprint","IMPRINT",EDGE,{"derivedFrom":sQuery(id+"F4.wireOp",EDGE,"E41.2.1")}),-1.0]])]});
            var Q7;
            Q7=makeQuery(id+"F4.imprint","IMPRINT",FACE,{"disambiguationData":[TD([[makeQuery(id+"F4.imprint","IMPRINT",EDGE,{"derivedFrom":sQuery(id+"F4.wireOp",EDGE,"E41.2.0")}),-1.0]])]});
            var Q8;
            Q8=makeQuery(id+"F4.imprint","IMPRINT",FACE,{"disambiguationData":[TD([[makeQuery(id+"F4.imprint","IMPRINT",EDGE,{"derivedFrom":sQuery(id+"F4.wireOp",EDGE,"E41.1.3")}),-1.0]])]});
            var Q9;
            Q9=makeQuery(id+"F4.imprint","IMPRINT",FACE,{"disambiguationData":[TD([[makeQuery(id+"F4.imprint","IMPRINT",EDGE,{"derivedFrom":sQuery(id+"F4.wireOp",EDGE,"E41.1.7")}),-1.0]])]});
            var Q10;
            Q10=makeQuery(id+"F4.imprint","IMPRINT",FACE,{"disambiguationData":[TD([[makeQuery(id+"F4.imprint","IMPRINT",EDGE,{"derivedFrom":sQuery(id+"F4.wireOp",EDGE,"E41.1.1")}),-1.0]])]});
            var Q11;
            Q11=makeQuery(id+"F4.imprint","IMPRINT",FACE,{"disambiguationData":[TD([[makeQuery(id+"F4.imprint","IMPRINT",EDGE,{"derivedFrom":sQuery(id+"F4.wireOp",EDGE,"E41.1.0")}),-1.0]])]});
            var Q12;
            Q12=makeQuery(id+"F4.imprint","IMPRINT",FACE,{"disambiguationData":[TD([[makeQuery(id+"F4.imprint","IMPRINT",EDGE,{"derivedFrom":sQuery(id+"F4.wireOp",EDGE,"E20")}),-1.0]])]});
            var Q13;
            Q13=makeQuery(id+"F4.imprint","IMPRINT",FACE,{"disambiguationData":[TD([[makeQuery(id+"F4.imprint","IMPRINT",EDGE,{"derivedFrom":sQuery(id+"F4.wireOp",EDGE,"E22")}),-1.0]])]});
            var Q14;
            Q14=makeQuery(id+"F4.imprint","IMPRINT",FACE,{"disambiguationData":[TD([[makeQuery(id+"F4.imprint","IMPRINT",EDGE,{"derivedFrom":sQuery(id+"F4.wireOp",EDGE,"E28")}),-1.0]])]});
            var Q15;
            Q15=makeQuery(id+"F4.imprint","IMPRINT",FACE,{"disambiguationData":[TD([[makeQuery(id+"F4.imprint","IMPRINT",EDGE,{"derivedFrom":sQuery(id+"F4.wireOp",EDGE,"E17")}),1.0]])]});
            extrude(context, id + "F5", {"entities" : qUnion([Q0, Q1, Q2, Q3, Q4, Q5, Q6, Q7, Q8, Q9, Q10, Q11, Q12, Q13, Q14, Q15]), "operationType" : NewBodyOperationType.REMOVE, "oppositeDirection" : true, "depth" : 4.5 * mm});
        }
        {
            var Q0;
            Q0=makeQuery(id+"F4.imprint","IMPRINT",FACE,{"disambiguationData":[TD([[makeQuery(id+"F4.imprint","IMPRINT",EDGE,{"derivedFrom":sQuery(id+"F4.wireOp",EDGE,"E41.3.2")}),1.0]])]});
            var Q1;
            Q1=makeQuery(id+"F4.imprint","IMPRINT",FACE,{"disambiguationData":[TD([[makeQuery(id+"F4.imprint","IMPRINT",EDGE,{"derivedFrom":sQuery(id+"F4.wireOp",EDGE,"E41.3.13")}),1.0]])]});
            var Q2;
            Q2=makeQuery(id+"F4.imprint","IMPRINT",FACE,{"disambiguationData":[TD([[makeQuery(id+"F4.imprint","IMPRINT",EDGE,{"derivedFrom":sQuery(id+"F4.wireOp",EDGE,"E26")}),-1.0]])]});
            var Q3;
            Q3=makeQuery(id+"F4.imprint","IMPRINT",FACE,{"disambiguationData":[TD([[makeQuery(id+"F4.imprint","IMPRINT",EDGE,{"derivedFrom":sQuery(id+"F4.wireOp",EDGE,"E24")}),-1.0]])]});
            var Q4;
            Q4=makeQuery(id+"F4.imprint","IMPRINT",FACE,{"disambiguationData":[TD([[makeQuery(id+"F4.imprint","IMPRINT",EDGE,{"derivedFrom":sQuery(id+"F4.wireOp",EDGE,"E41.1.13")}),1.0]])]});
            var Q5;
            Q5=makeQuery(id+"F4.imprint","IMPRINT",FACE,{"disambiguationData":[TD([[makeQuery(id+"F4.imprint","IMPRINT",EDGE,{"derivedFrom":sQuery(id+"F4.wireOp",EDGE,"E41.1.2")}),1.0]])]});
            var Q6;
            Q6=makeQuery(id+"F4.imprint","IMPRINT",FACE,{"disambiguationData":[TD([[makeQuery(id+"F4.imprint","IMPRINT",EDGE,{"derivedFrom":sQuery(id+"F4.wireOp",EDGE,"E41.2.13")}),1.0]])]});
            var Q7;
            Q7=makeQuery(id+"F4.imprint","IMPRINT",FACE,{"disambiguationData":[TD([[makeQuery(id+"F4.imprint","IMPRINT",EDGE,{"derivedFrom":sQuery(id+"F4.wireOp",EDGE,"E41.2.2")}),1.0]])]});
            extrude(context, id + "F6", {"entities" : qUnion([Q0, Q1, Q2, Q3, Q4, Q5, Q6, Q7]), "operationType" : NewBodyOperationType.REMOVE, "oppositeDirection" : true, "depth" : 2.5 * mm});
        }
        {
            var Q0;
            Q0=makeQuery(id+"F5.boolean.opBoolean","COPY",EDGE,{"derivedFrom":makeQuery(id+"F5.opExtrude","SWEPT_EDGE",EDGE,{"disambiguationData":[OSD([sQuery(id+"F4.wireOp",EDGE,"E41.3.4"),sQuery(id+"F4.wireOp",EDGE,"E41.3.10")])]})});
            var Q1;
            Q1=makeQuery(id+"F5.boolean.opBoolean","COPY",EDGE,{"derivedFrom":makeQuery(id+"F5.opExtrude","SWEPT_EDGE",EDGE,{"disambiguationData":[OSD([sQuery(id+"F4.wireOp",EDGE,"E41.3.1"),sQuery(id+"F4.wireOp",EDGE,"E41.3.11")])]})});
            var Q2;
            Q2=makeQuery(id+"F6.boolean.opBoolean","COPY",EDGE,{"derivedFrom":makeQuery(id+"F6.opExtrude","SWEPT_EDGE",EDGE,{"disambiguationData":[OSD([sQuery(id+"F4.wireOp",EDGE,"E41.3.13"),sQuery(id+"F4.wireOp",EDGE,"E41.3.15")])]})});
            var Q3;
            Q3=makeQuery(id+"F6.boolean.opBoolean","COPY",EDGE,{"derivedFrom":makeQuery(id+"F6.opExtrude","SWEPT_EDGE",EDGE,{"disambiguationData":[OSD([sQuery(id+"F4.wireOp",EDGE,"E41.3.2"),sQuery(id+"F4.wireOp",EDGE,"E41.3.19")])]})});
            var Q4;
            Q4=makeQuery(id+"F5.boolean.opBoolean","COPY",EDGE,{"derivedFrom":makeQuery(id+"F5.opExtrude","SWEPT_EDGE",EDGE,{"disambiguationData":[OSD([sQuery(id+"F4.wireOp",EDGE,"E41.3.7"),sQuery(id+"F4.wireOp",EDGE,"E41.3.14")])]})});
            var Q5;
            Q5=makeQuery(id+"F5.boolean.opBoolean","COPY",EDGE,{"derivedFrom":makeQuery(id+"F5.opExtrude","SWEPT_EDGE",EDGE,{"disambiguationData":[OSD([sQuery(id+"F4.wireOp",EDGE,"E41.3.3"),sQuery(id+"F4.wireOp",EDGE,"E41.3.20")])]})});
            var Q6;
            Q6=makeQuery(id+"F5.boolean.opBoolean","COPY",EDGE,{"derivedFrom":makeQuery(id+"F5.opExtrude","SWEPT_EDGE",EDGE,{"disambiguationData":[OSD([sQuery(id+"F4.wireOp",EDGE,"E41.2.4"),sQuery(id+"F4.wireOp",EDGE,"E41.2.10")])]})});
            var Q7;
            Q7=makeQuery(id+"F5.boolean.opBoolean","COPY",EDGE,{"derivedFrom":makeQuery(id+"F5.opExtrude","SWEPT_EDGE",EDGE,{"disambiguationData":[OSD([sQuery(id+"F4.wireOp",EDGE,"E41.2.1"),sQuery(id+"F4.wireOp",EDGE,"E41.2.11")])]})});
            var Q8;
            Q8=makeQuery(id+"F6.boolean.opBoolean","COPY",EDGE,{"derivedFrom":makeQuery(id+"F6.opExtrude","SWEPT_EDGE",EDGE,{"disambiguationData":[OSD([sQuery(id+"F4.wireOp",EDGE,"E41.2.13"),sQuery(id+"F4.wireOp",EDGE,"E41.2.15")])]})});
            var Q9;
            Q9=makeQuery(id+"F6.boolean.opBoolean","COPY",EDGE,{"derivedFrom":makeQuery(id+"F6.opExtrude","SWEPT_EDGE",EDGE,{"disambiguationData":[OSD([sQuery(id+"F4.wireOp",EDGE,"E41.2.2"),sQuery(id+"F4.wireOp",EDGE,"E41.2.19")])]})});
            var Q10;
            Q10=makeQuery(id+"F5.boolean.opBoolean","COPY",EDGE,{"derivedFrom":makeQuery(id+"F5.opExtrude","SWEPT_EDGE",EDGE,{"disambiguationData":[OSD([sQuery(id+"F4.wireOp",EDGE,"E41.2.7"),sQuery(id+"F4.wireOp",EDGE,"E41.2.14")])]})});
            var Q11;
            Q11=makeQuery(id+"F5.boolean.opBoolean","COPY",EDGE,{"derivedFrom":makeQuery(id+"F5.opExtrude","SWEPT_EDGE",EDGE,{"disambiguationData":[OSD([sQuery(id+"F4.wireOp",EDGE,"E41.2.3"),sQuery(id+"F4.wireOp",EDGE,"E41.2.20")])]})});
            var Q12;
            Q12=makeQuery(id+"F5.boolean.opBoolean","COPY",EDGE,{"derivedFrom":makeQuery(id+"F5.opExtrude","SWEPT_EDGE",EDGE,{"disambiguationData":[OSD([sQuery(id+"F4.wireOp",EDGE,"E41.1.3"),sQuery(id+"F4.wireOp",EDGE,"E41.1.20")])]})});
            var Q13;
            Q13=makeQuery(id+"F5.boolean.opBoolean","COPY",EDGE,{"derivedFrom":makeQuery(id+"F5.opExtrude","SWEPT_EDGE",EDGE,{"disambiguationData":[OSD([sQuery(id+"F4.wireOp",EDGE,"E41.1.7"),sQuery(id+"F4.wireOp",EDGE,"E41.1.14")])]})});
            var Q14;
            Q14=makeQuery(id+"F6.boolean.opBoolean","COPY",EDGE,{"derivedFrom":makeQuery(id+"F6.opExtrude","SWEPT_EDGE",EDGE,{"disambiguationData":[OSD([sQuery(id+"F4.wireOp",EDGE,"E41.1.2"),sQuery(id+"F4.wireOp",EDGE,"E41.1.19")])]})});
            var Q15;
            Q15=makeQuery(id+"F6.boolean.opBoolean","COPY",EDGE,{"derivedFrom":makeQuery(id+"F6.opExtrude","SWEPT_EDGE",EDGE,{"disambiguationData":[OSD([sQuery(id+"F4.wireOp",EDGE,"E41.1.13"),sQuery(id+"F4.wireOp",EDGE,"E41.1.15")])]})});
            var Q16;
            Q16=makeQuery(id+"F5.boolean.opBoolean","COPY",EDGE,{"derivedFrom":makeQuery(id+"F5.opExtrude","SWEPT_EDGE",EDGE,{"disambiguationData":[OSD([sQuery(id+"F4.wireOp",EDGE,"E41.1.1"),sQuery(id+"F4.wireOp",EDGE,"E41.1.11")])]})});
            var Q17;
            Q17=makeQuery(id+"F5.boolean.opBoolean","COPY",EDGE,{"derivedFrom":makeQuery(id+"F5.opExtrude","SWEPT_EDGE",EDGE,{"disambiguationData":[OSD([sQuery(id+"F4.wireOp",EDGE,"E41.1.4"),sQuery(id+"F4.wireOp",EDGE,"E41.1.10")])]})});
            var Q18;
            Q18=makeQuery(id+"F5.boolean.opBoolean","COPY",EDGE,{"derivedFrom":makeQuery(id+"F5.opExtrude","SWEPT_EDGE",EDGE,{"disambiguationData":[OSD([sQuery(id+"F4.wireOp",EDGE,"E20"),sQuery(id+"F4.wireOp",EDGE,"E39.trimOffspring")])]})});
            var Q19;
            Q19=makeQuery(id+"F5.boolean.opBoolean","COPY",EDGE,{"derivedFrom":makeQuery(id+"F5.opExtrude","SWEPT_EDGE",EDGE,{"disambiguationData":[OSD([sQuery(id+"F4.wireOp",EDGE,"E22"),sQuery(id+"F4.wireOp",EDGE,"E40.trimOffspring")])]})});
            var Q20;
            Q20=makeQuery(id+"F6.boolean.opBoolean","COPY",EDGE,{"derivedFrom":makeQuery(id+"F6.opExtrude","SWEPT_EDGE",EDGE,{"disambiguationData":[OSD([sQuery(id+"F4.wireOp",EDGE,"E24"),sQuery(id+"F4.wireOp",EDGE,"E35.trimOffspring")])]})});
            var Q21;
            Q21=makeQuery(id+"F6.boolean.opBoolean","COPY",EDGE,{"derivedFrom":makeQuery(id+"F6.opExtrude","SWEPT_EDGE",EDGE,{"disambiguationData":[OSD([sQuery(id+"F4.wireOp",EDGE,"E26"),sQuery(id+"F4.wireOp",EDGE,"E33.trimOffspring")])]})});
            var Q22;
            Q22=makeQuery(id+"F5.boolean.opBoolean","COPY",EDGE,{"derivedFrom":makeQuery(id+"F5.opExtrude","SWEPT_EDGE",EDGE,{"disambiguationData":[OSD([sQuery(id+"F4.wireOp",EDGE,"E28"),sQuery(id+"F4.wireOp",EDGE,"E32.trimOffspring")])]})});
            var Q23;
            Q23=makeQuery(id+"F5.boolean.opBoolean","COPY",EDGE,{"derivedFrom":makeQuery(id+"F5.opExtrude","SWEPT_EDGE",EDGE,{"disambiguationData":[OSD([sQuery(id+"F4.wireOp",EDGE,"E17"),sQuery(id+"F4.wireOp",EDGE,"E30")])]})});
            var Q24;
            Q24=makeQuery(id+"F5.boolean.opBoolean","COPY",EDGE,{"derivedFrom":makeQuery(id+"F5.opExtrude","SWEPT_EDGE",EDGE,{"disambiguationData":[OSD([sQuery(id+"F4.wireOp",EDGE,"E41.3.6"),sQuery(id+"F4.wireOp",EDGE,"E41.3.22")])]})});
            var Q25;
            Q25=makeQuery(id+"F5.boolean.opBoolean","COPY",EDGE,{"derivedFrom":makeQuery(id+"F5.opExtrude","SWEPT_EDGE",EDGE,{"disambiguationData":[OSD([sQuery(id+"F4.wireOp",EDGE,"E41.3.12"),sQuery(id+"F4.wireOp",EDGE,"E41.3.16")])]})});
            var Q26;
            Q26=makeQuery(id+"F6.boolean.opBoolean","COPY",EDGE,{"derivedFrom":makeQuery(id+"F6.opExtrude","SWEPT_EDGE",EDGE,{"disambiguationData":[OSD([sQuery(id+"F4.wireOp",EDGE,"E41.3.9"),sQuery(id+"F4.wireOp",EDGE,"E41.3.17")])]})});
            var Q27;
            Q27=makeQuery(id+"F6.boolean.opBoolean","COPY",EDGE,{"derivedFrom":makeQuery(id+"F6.opExtrude","SWEPT_EDGE",EDGE,{"disambiguationData":[OSD([sQuery(id+"F4.wireOp",EDGE,"E41.3.18"),sQuery(id+"F4.wireOp",EDGE,"E41.3.23")])]})});
            var Q28;
            Q28=makeQuery(id+"F5.boolean.opBoolean","COPY",EDGE,{"derivedFrom":makeQuery(id+"F5.opExtrude","SWEPT_EDGE",EDGE,{"disambiguationData":[OSD([sQuery(id+"F4.wireOp",EDGE,"E41.3.5"),sQuery(id+"F4.wireOp",EDGE,"E41.3.21")])]})});
            var Q29;
            Q29=makeQuery(id+"F5.boolean.opBoolean","COPY",EDGE,{"derivedFrom":makeQuery(id+"F5.opExtrude","SWEPT_EDGE",EDGE,{"disambiguationData":[OSD([sQuery(id+"F4.wireOp",EDGE,"E41.3.0"),sQuery(id+"F4.wireOp",EDGE,"E41.3.8")])]})});
            var Q30;
            Q30=makeQuery(id+"F5.boolean.opBoolean","COPY",EDGE,{"derivedFrom":makeQuery(id+"F5.opExtrude","SWEPT_EDGE",EDGE,{"disambiguationData":[OSD([sQuery(id+"F4.wireOp",EDGE,"E41.2.6"),sQuery(id+"F4.wireOp",EDGE,"E41.2.22")])]})});
            var Q31;
            Q31=makeQuery(id+"F5.boolean.opBoolean","COPY",EDGE,{"derivedFrom":makeQuery(id+"F5.opExtrude","SWEPT_EDGE",EDGE,{"disambiguationData":[OSD([sQuery(id+"F4.wireOp",EDGE,"E41.2.12"),sQuery(id+"F4.wireOp",EDGE,"E41.2.16")])]})});
            var Q32;
            Q32=makeQuery(id+"F6.boolean.opBoolean","COPY",EDGE,{"derivedFrom":makeQuery(id+"F6.opExtrude","SWEPT_EDGE",EDGE,{"disambiguationData":[OSD([sQuery(id+"F4.wireOp",EDGE,"E41.2.9"),sQuery(id+"F4.wireOp",EDGE,"E41.2.17")])]})});
            var Q33;
            Q33=makeQuery(id+"F6.boolean.opBoolean","COPY",EDGE,{"derivedFrom":makeQuery(id+"F6.opExtrude","SWEPT_EDGE",EDGE,{"disambiguationData":[OSD([sQuery(id+"F4.wireOp",EDGE,"E41.2.18"),sQuery(id+"F4.wireOp",EDGE,"E41.2.23")])]})});
            var Q34;
            Q34=makeQuery(id+"F5.boolean.opBoolean","COPY",EDGE,{"derivedFrom":makeQuery(id+"F5.opExtrude","SWEPT_EDGE",EDGE,{"disambiguationData":[OSD([sQuery(id+"F4.wireOp",EDGE,"E41.2.5"),sQuery(id+"F4.wireOp",EDGE,"E41.2.21")])]})});
            var Q35;
            Q35=makeQuery(id+"F5.boolean.opBoolean","COPY",EDGE,{"derivedFrom":makeQuery(id+"F5.opExtrude","SWEPT_EDGE",EDGE,{"disambiguationData":[OSD([sQuery(id+"F4.wireOp",EDGE,"E41.2.0"),sQuery(id+"F4.wireOp",EDGE,"E41.2.8")])]})});
            var Q36;
            Q36=makeQuery(id+"F5.boolean.opBoolean","COPY",EDGE,{"derivedFrom":makeQuery(id+"F5.opExtrude","SWEPT_EDGE",EDGE,{"disambiguationData":[OSD([sQuery(id+"F4.wireOp",EDGE,"E41.1.6"),sQuery(id+"F4.wireOp",EDGE,"E41.1.22")])]})});
            var Q37;
            Q37=makeQuery(id+"F5.boolean.opBoolean","COPY",EDGE,{"derivedFrom":makeQuery(id+"F5.opExtrude","SWEPT_EDGE",EDGE,{"disambiguationData":[OSD([sQuery(id+"F4.wireOp",EDGE,"E41.1.12"),sQuery(id+"F4.wireOp",EDGE,"E41.1.16")])]})});
            var Q38;
            Q38=makeQuery(id+"F6.boolean.opBoolean","COPY",EDGE,{"derivedFrom":makeQuery(id+"F6.opExtrude","SWEPT_EDGE",EDGE,{"disambiguationData":[OSD([sQuery(id+"F4.wireOp",EDGE,"E41.1.9"),sQuery(id+"F4.wireOp",EDGE,"E41.1.17")])]})});
            var Q39;
            Q39=makeQuery(id+"F6.boolean.opBoolean","COPY",EDGE,{"derivedFrom":makeQuery(id+"F6.opExtrude","SWEPT_EDGE",EDGE,{"disambiguationData":[OSD([sQuery(id+"F4.wireOp",EDGE,"E41.1.18"),sQuery(id+"F4.wireOp",EDGE,"E41.1.23")])]})});
            var Q40;
            Q40=makeQuery(id+"F5.boolean.opBoolean","COPY",EDGE,{"derivedFrom":makeQuery(id+"F5.opExtrude","SWEPT_EDGE",EDGE,{"disambiguationData":[OSD([sQuery(id+"F4.wireOp",EDGE,"E41.1.5"),sQuery(id+"F4.wireOp",EDGE,"E41.1.21")])]})});
            var Q41;
            Q41=makeQuery(id+"F5.boolean.opBoolean","COPY",EDGE,{"derivedFrom":makeQuery(id+"F5.opExtrude","SWEPT_EDGE",EDGE,{"disambiguationData":[OSD([sQuery(id+"F4.wireOp",EDGE,"E41.1.0"),sQuery(id+"F4.wireOp",EDGE,"E41.1.8")])]})});
            var Q42;
            Q42=makeQuery(id+"F5.boolean.opBoolean","COPY",EDGE,{"derivedFrom":makeQuery(id+"F5.opExtrude","SWEPT_EDGE",EDGE,{"disambiguationData":[OSD([sQuery(id+"F4.wireOp",EDGE,"E21"),sQuery(id+"F4.wireOp",EDGE,"E38.trimOffspring")])]})});
            var Q43;
            Q43=makeQuery(id+"F5.boolean.opBoolean","COPY",EDGE,{"derivedFrom":makeQuery(id+"F5.opExtrude","SWEPT_EDGE",EDGE,{"disambiguationData":[OSD([sQuery(id+"F4.wireOp",EDGE,"E23"),sQuery(id+"F4.wireOp",EDGE,"E37.trimOffspring")])]})});
            var Q44;
            Q44=makeQuery(id+"F6.boolean.opBoolean","COPY",EDGE,{"derivedFrom":makeQuery(id+"F6.opExtrude","SWEPT_EDGE",EDGE,{"disambiguationData":[OSD([sQuery(id+"F4.wireOp",EDGE,"E25"),sQuery(id+"F4.wireOp",EDGE,"E36.trimOffspring")])]})});
            var Q45;
            Q45=makeQuery(id+"F6.boolean.opBoolean","COPY",EDGE,{"derivedFrom":makeQuery(id+"F6.opExtrude","SWEPT_EDGE",EDGE,{"disambiguationData":[OSD([sQuery(id+"F4.wireOp",EDGE,"E27"),sQuery(id+"F4.wireOp",EDGE,"E34.trimOffspring")])]})});
            var Q46;
            Q46=makeQuery(id+"F5.boolean.opBoolean","COPY",EDGE,{"derivedFrom":makeQuery(id+"F5.opExtrude","SWEPT_EDGE",EDGE,{"disambiguationData":[OSD([sQuery(id+"F4.wireOp",EDGE,"E29"),sQuery(id+"F4.wireOp",EDGE,"E31.trimOffspring")])]})});
            var Q47;
            Q47=makeQuery(id+"F5.boolean.opBoolean","COPY",EDGE,{"derivedFrom":makeQuery(id+"F5.opExtrude","SWEPT_EDGE",EDGE,{"disambiguationData":[OSD([sQuery(id+"F4.wireOp",EDGE,"E18"),sQuery(id+"F4.wireOp",EDGE,"E19")])]})});
            var Q48;
            Q48=makeQuery(id+"F5.boolean.opBoolean","COPY",EDGE,{"derivedFrom":makeQuery(id+"F5.opExtrude","SWEPT_EDGE",EDGE,{"disambiguationData":[OSD([sQuery(id+"F4.wireOp",EDGE,"E41.3.1"),sQuery(id+"F4.wireOp",EDGE,"E41.3.5")])]})});
            var Q49;
            Q49=makeQuery(id+"F6.boolean.opBoolean","COPY",EDGE,{"derivedFrom":makeQuery(id+"F6.opExtrude","SWEPT_EDGE",EDGE,{"disambiguationData":[OSD([sQuery(id+"F4.wireOp",EDGE,"E41.3.15"),sQuery(id+"F4.wireOp",EDGE,"E41.3.23")])]})});
            var Q50;
            Q50=makeQuery(id+"F6.boolean.opBoolean","COPY",EDGE,{"derivedFrom":makeQuery(id+"F6.opExtrude","SWEPT_EDGE",EDGE,{"disambiguationData":[OSD([sQuery(id+"F4.wireOp",EDGE,"E41.3.9"),sQuery(id+"F4.wireOp",EDGE,"E41.3.19")])]})});
            var Q51;
            Q51=makeQuery(id+"F5.boolean.opBoolean","COPY",EDGE,{"derivedFrom":makeQuery(id+"F5.opExtrude","SWEPT_EDGE",EDGE,{"disambiguationData":[OSD([sQuery(id+"F4.wireOp",EDGE,"E41.3.7"),sQuery(id+"F4.wireOp",EDGE,"E41.3.12")])]})});
            var Q52;
            Q52=makeQuery(id+"F5.boolean.opBoolean","COPY",EDGE,{"derivedFrom":makeQuery(id+"F5.opExtrude","SWEPT_EDGE",EDGE,{"disambiguationData":[OSD([sQuery(id+"F4.wireOp",EDGE,"E41.3.3"),sQuery(id+"F4.wireOp",EDGE,"E41.3.22")])]})});
            var Q53;
            Q53=makeQuery(id+"F5.boolean.opBoolean","COPY",EDGE,{"derivedFrom":makeQuery(id+"F5.opExtrude","SWEPT_EDGE",EDGE,{"disambiguationData":[OSD([sQuery(id+"F4.wireOp",EDGE,"E41.3.0"),sQuery(id+"F4.wireOp",EDGE,"E41.3.4")])]})});
            var Q54;
            Q54=makeQuery(id+"F5.boolean.opBoolean","COPY",EDGE,{"derivedFrom":makeQuery(id+"F5.opExtrude","SWEPT_EDGE",EDGE,{"disambiguationData":[OSD([sQuery(id+"F4.wireOp",EDGE,"E41.2.3"),sQuery(id+"F4.wireOp",EDGE,"E41.2.22")])]})});
            var Q55;
            Q55=makeQuery(id+"F5.boolean.opBoolean","COPY",EDGE,{"derivedFrom":makeQuery(id+"F5.opExtrude","SWEPT_EDGE",EDGE,{"disambiguationData":[OSD([sQuery(id+"F4.wireOp",EDGE,"E41.2.7"),sQuery(id+"F4.wireOp",EDGE,"E41.2.12")])]})});
            var Q56;
            Q56=makeQuery(id+"F6.boolean.opBoolean","COPY",EDGE,{"derivedFrom":makeQuery(id+"F6.opExtrude","SWEPT_EDGE",EDGE,{"disambiguationData":[OSD([sQuery(id+"F4.wireOp",EDGE,"E41.2.9"),sQuery(id+"F4.wireOp",EDGE,"E41.2.19")])]})});
            var Q57;
            Q57=makeQuery(id+"F6.boolean.opBoolean","COPY",EDGE,{"derivedFrom":makeQuery(id+"F6.opExtrude","SWEPT_EDGE",EDGE,{"disambiguationData":[OSD([sQuery(id+"F4.wireOp",EDGE,"E41.2.15"),sQuery(id+"F4.wireOp",EDGE,"E41.2.23")])]})});
            var Q58;
            Q58=makeQuery(id+"F5.boolean.opBoolean","COPY",EDGE,{"derivedFrom":makeQuery(id+"F5.opExtrude","SWEPT_EDGE",EDGE,{"disambiguationData":[OSD([sQuery(id+"F4.wireOp",EDGE,"E41.2.1"),sQuery(id+"F4.wireOp",EDGE,"E41.2.5")])]})});
            var Q59;
            Q59=makeQuery(id+"F5.boolean.opBoolean","COPY",EDGE,{"derivedFrom":makeQuery(id+"F5.opExtrude","SWEPT_EDGE",EDGE,{"disambiguationData":[OSD([sQuery(id+"F4.wireOp",EDGE,"E41.2.0"),sQuery(id+"F4.wireOp",EDGE,"E41.2.4")])]})});
            var Q60;
            Q60=makeQuery(id+"F5.boolean.opBoolean","COPY",EDGE,{"derivedFrom":makeQuery(id+"F5.opExtrude","SWEPT_EDGE",EDGE,{"disambiguationData":[OSD([sQuery(id+"F4.wireOp",EDGE,"E41.1.7"),sQuery(id+"F4.wireOp",EDGE,"E41.1.12")])]})});
            var Q61;
            Q61=makeQuery(id+"F5.boolean.opBoolean","COPY",EDGE,{"derivedFrom":makeQuery(id+"F5.opExtrude","SWEPT_EDGE",EDGE,{"disambiguationData":[OSD([sQuery(id+"F4.wireOp",EDGE,"E41.1.3"),sQuery(id+"F4.wireOp",EDGE,"E41.1.22")])]})});
            var Q62;
            Q62=makeQuery(id+"F6.boolean.opBoolean","COPY",EDGE,{"derivedFrom":makeQuery(id+"F6.opExtrude","SWEPT_EDGE",EDGE,{"disambiguationData":[OSD([sQuery(id+"F4.wireOp",EDGE,"E41.1.9"),sQuery(id+"F4.wireOp",EDGE,"E41.1.19")])]})});
            var Q63;
            Q63=makeQuery(id+"F6.boolean.opBoolean","COPY",EDGE,{"derivedFrom":makeQuery(id+"F6.opExtrude","SWEPT_EDGE",EDGE,{"disambiguationData":[OSD([sQuery(id+"F4.wireOp",EDGE,"E41.1.15"),sQuery(id+"F4.wireOp",EDGE,"E41.1.23")])]})});
            var Q64;
            Q64=makeQuery(id+"F5.boolean.opBoolean","COPY",EDGE,{"derivedFrom":makeQuery(id+"F5.opExtrude","SWEPT_EDGE",EDGE,{"disambiguationData":[OSD([sQuery(id+"F4.wireOp",EDGE,"E41.1.1"),sQuery(id+"F4.wireOp",EDGE,"E41.1.5")])]})});
            var Q65;
            Q65=makeQuery(id+"F5.boolean.opBoolean","COPY",EDGE,{"derivedFrom":makeQuery(id+"F5.opExtrude","SWEPT_EDGE",EDGE,{"disambiguationData":[OSD([sQuery(id+"F4.wireOp",EDGE,"E41.1.0"),sQuery(id+"F4.wireOp",EDGE,"E41.1.4")])]})});
            var Q66;
            Q66=makeQuery(id+"F5.boolean.opBoolean","COPY",EDGE,{"derivedFrom":makeQuery(id+"F5.opExtrude","SWEPT_EDGE",EDGE,{"disambiguationData":[OSD([sQuery(id+"F4.wireOp",EDGE,"E20"),sQuery(id+"F4.wireOp",EDGE,"E38.trimOffspring")])]})});
            var Q67;
            Q67=makeQuery(id+"F5.boolean.opBoolean","COPY",EDGE,{"derivedFrom":makeQuery(id+"F5.opExtrude","SWEPT_EDGE",EDGE,{"disambiguationData":[OSD([sQuery(id+"F4.wireOp",EDGE,"E22"),sQuery(id+"F4.wireOp",EDGE,"E37.trimOffspring")])]})});
            var Q68;
            Q68=makeQuery(id+"F6.boolean.opBoolean","COPY",EDGE,{"derivedFrom":makeQuery(id+"F6.opExtrude","SWEPT_EDGE",EDGE,{"disambiguationData":[OSD([sQuery(id+"F4.wireOp",EDGE,"E24"),sQuery(id+"F4.wireOp",EDGE,"E36.trimOffspring")])]})});
            var Q69;
            Q69=makeQuery(id+"F6.boolean.opBoolean","COPY",EDGE,{"derivedFrom":makeQuery(id+"F6.opExtrude","SWEPT_EDGE",EDGE,{"disambiguationData":[OSD([sQuery(id+"F4.wireOp",EDGE,"E26"),sQuery(id+"F4.wireOp",EDGE,"E34.trimOffspring")])]})});
            var Q70;
            Q70=makeQuery(id+"F5.boolean.opBoolean","COPY",EDGE,{"derivedFrom":makeQuery(id+"F5.opExtrude","SWEPT_EDGE",EDGE,{"disambiguationData":[OSD([sQuery(id+"F4.wireOp",EDGE,"E28"),sQuery(id+"F4.wireOp",EDGE,"E31.trimOffspring")])]})});
            var Q71;
            Q71=makeQuery(id+"F5.boolean.opBoolean","COPY",EDGE,{"derivedFrom":makeQuery(id+"F5.opExtrude","SWEPT_EDGE",EDGE,{"disambiguationData":[OSD([sQuery(id+"F4.wireOp",EDGE,"E18"),sQuery(id+"F4.wireOp",EDGE,"E30")])]})});
            var Q72;
            Q72=makeQuery(id+"F5.boolean.opBoolean","COPY",EDGE,{"derivedFrom":makeQuery(id+"F5.opExtrude","SWEPT_EDGE",EDGE,{"disambiguationData":[OSD([sQuery(id+"F4.wireOp",EDGE,"E41.3.6"),sQuery(id+"F4.wireOp",EDGE,"E41.3.20")])]})});
            var Q73;
            Q73=makeQuery(id+"F5.boolean.opBoolean","COPY",EDGE,{"derivedFrom":makeQuery(id+"F5.opExtrude","SWEPT_EDGE",EDGE,{"disambiguationData":[OSD([sQuery(id+"F4.wireOp",EDGE,"E41.3.14"),sQuery(id+"F4.wireOp",EDGE,"E41.3.16")])]})});
            var Q74;
            Q74=makeQuery(id+"F6.boolean.opBoolean","COPY",EDGE,{"derivedFrom":makeQuery(id+"F6.opExtrude","SWEPT_EDGE",EDGE,{"disambiguationData":[OSD([sQuery(id+"F4.wireOp",EDGE,"E41.3.2"),sQuery(id+"F4.wireOp",EDGE,"E41.3.17")])]})});
            var Q75;
            Q75=makeQuery(id+"F6.boolean.opBoolean","COPY",EDGE,{"derivedFrom":makeQuery(id+"F6.opExtrude","SWEPT_EDGE",EDGE,{"disambiguationData":[OSD([sQuery(id+"F4.wireOp",EDGE,"E41.3.13"),sQuery(id+"F4.wireOp",EDGE,"E41.3.18")])]})});
            var Q76;
            Q76=makeQuery(id+"F5.boolean.opBoolean","COPY",EDGE,{"derivedFrom":makeQuery(id+"F5.opExtrude","SWEPT_EDGE",EDGE,{"disambiguationData":[OSD([sQuery(id+"F4.wireOp",EDGE,"E41.3.8"),sQuery(id+"F4.wireOp",EDGE,"E41.3.10")])]})});
            var Q77;
            Q77=makeQuery(id+"F5.boolean.opBoolean","COPY",EDGE,{"derivedFrom":makeQuery(id+"F5.opExtrude","SWEPT_EDGE",EDGE,{"disambiguationData":[OSD([sQuery(id+"F4.wireOp",EDGE,"E41.3.11"),sQuery(id+"F4.wireOp",EDGE,"E41.3.21")])]})});
            var Q78;
            Q78=makeQuery(id+"F5.boolean.opBoolean","COPY",EDGE,{"derivedFrom":makeQuery(id+"F5.opExtrude","SWEPT_EDGE",EDGE,{"disambiguationData":[OSD([sQuery(id+"F4.wireOp",EDGE,"E41.2.6"),sQuery(id+"F4.wireOp",EDGE,"E41.2.20")])]})});
            var Q79;
            Q79=makeQuery(id+"F5.boolean.opBoolean","COPY",EDGE,{"derivedFrom":makeQuery(id+"F5.opExtrude","SWEPT_EDGE",EDGE,{"disambiguationData":[OSD([sQuery(id+"F4.wireOp",EDGE,"E41.2.14"),sQuery(id+"F4.wireOp",EDGE,"E41.2.16")])]})});
            var Q80;
            Q80=makeQuery(id+"F6.boolean.opBoolean","COPY",EDGE,{"derivedFrom":makeQuery(id+"F6.opExtrude","SWEPT_EDGE",EDGE,{"disambiguationData":[OSD([sQuery(id+"F4.wireOp",EDGE,"E41.2.2"),sQuery(id+"F4.wireOp",EDGE,"E41.2.17")])]})});
            var Q81;
            Q81=makeQuery(id+"F6.boolean.opBoolean","COPY",EDGE,{"derivedFrom":makeQuery(id+"F6.opExtrude","SWEPT_EDGE",EDGE,{"disambiguationData":[OSD([sQuery(id+"F4.wireOp",EDGE,"E41.2.13"),sQuery(id+"F4.wireOp",EDGE,"E41.2.18")])]})});
            var Q82;
            Q82=makeQuery(id+"F5.boolean.opBoolean","COPY",EDGE,{"derivedFrom":makeQuery(id+"F5.opExtrude","SWEPT_EDGE",EDGE,{"disambiguationData":[OSD([sQuery(id+"F4.wireOp",EDGE,"E41.2.11"),sQuery(id+"F4.wireOp",EDGE,"E41.2.21")])]})});
            var Q83;
            Q83=makeQuery(id+"F5.boolean.opBoolean","COPY",EDGE,{"derivedFrom":makeQuery(id+"F5.opExtrude","SWEPT_EDGE",EDGE,{"disambiguationData":[OSD([sQuery(id+"F4.wireOp",EDGE,"E41.2.8"),sQuery(id+"F4.wireOp",EDGE,"E41.2.10")])]})});
            var Q84;
            Q84=makeQuery(id+"F5.boolean.opBoolean","COPY",EDGE,{"derivedFrom":makeQuery(id+"F5.opExtrude","SWEPT_EDGE",EDGE,{"disambiguationData":[OSD([sQuery(id+"F4.wireOp",EDGE,"E41.1.6"),sQuery(id+"F4.wireOp",EDGE,"E41.1.20")])]})});
            var Q85;
            Q85=makeQuery(id+"F5.boolean.opBoolean","COPY",EDGE,{"derivedFrom":makeQuery(id+"F5.opExtrude","SWEPT_EDGE",EDGE,{"disambiguationData":[OSD([sQuery(id+"F4.wireOp",EDGE,"E41.1.14"),sQuery(id+"F4.wireOp",EDGE,"E41.1.16")])]})});
            var Q86;
            Q86=makeQuery(id+"F6.boolean.opBoolean","COPY",EDGE,{"derivedFrom":makeQuery(id+"F6.opExtrude","SWEPT_EDGE",EDGE,{"disambiguationData":[OSD([sQuery(id+"F4.wireOp",EDGE,"E41.1.2"),sQuery(id+"F4.wireOp",EDGE,"E41.1.17")])]})});
            var Q87;
            Q87=makeQuery(id+"F6.boolean.opBoolean","COPY",EDGE,{"derivedFrom":makeQuery(id+"F6.opExtrude","SWEPT_EDGE",EDGE,{"disambiguationData":[OSD([sQuery(id+"F4.wireOp",EDGE,"E41.1.13"),sQuery(id+"F4.wireOp",EDGE,"E41.1.18")])]})});
            var Q88;
            Q88=makeQuery(id+"F5.boolean.opBoolean","COPY",EDGE,{"derivedFrom":makeQuery(id+"F5.opExtrude","SWEPT_EDGE",EDGE,{"disambiguationData":[OSD([sQuery(id+"F4.wireOp",EDGE,"E41.1.11"),sQuery(id+"F4.wireOp",EDGE,"E41.1.21")])]})});
            var Q89;
            Q89=makeQuery(id+"F5.boolean.opBoolean","COPY",EDGE,{"derivedFrom":makeQuery(id+"F5.opExtrude","SWEPT_EDGE",EDGE,{"disambiguationData":[OSD([sQuery(id+"F4.wireOp",EDGE,"E41.1.8"),sQuery(id+"F4.wireOp",EDGE,"E41.1.10")])]})});
            var Q90;
            Q90=makeQuery(id+"F5.boolean.opBoolean","COPY",EDGE,{"derivedFrom":makeQuery(id+"F5.opExtrude","SWEPT_EDGE",EDGE,{"disambiguationData":[OSD([sQuery(id+"F4.wireOp",EDGE,"E21"),sQuery(id+"F4.wireOp",EDGE,"E39.trimOffspring")])]})});
            var Q91;
            Q91=makeQuery(id+"F5.boolean.opBoolean","COPY",EDGE,{"derivedFrom":makeQuery(id+"F5.opExtrude","SWEPT_EDGE",EDGE,{"disambiguationData":[OSD([sQuery(id+"F4.wireOp",EDGE,"E23"),sQuery(id+"F4.wireOp",EDGE,"E40.trimOffspring")])]})});
            var Q92;
            Q92=makeQuery(id+"F6.boolean.opBoolean","COPY",EDGE,{"derivedFrom":makeQuery(id+"F6.opExtrude","SWEPT_EDGE",EDGE,{"disambiguationData":[OSD([sQuery(id+"F4.wireOp",EDGE,"E25"),sQuery(id+"F4.wireOp",EDGE,"E35.trimOffspring")])]})});
            var Q93;
            Q93=makeQuery(id+"F6.boolean.opBoolean","COPY",EDGE,{"derivedFrom":makeQuery(id+"F6.opExtrude","SWEPT_EDGE",EDGE,{"disambiguationData":[OSD([sQuery(id+"F4.wireOp",EDGE,"E27"),sQuery(id+"F4.wireOp",EDGE,"E33.trimOffspring")])]})});
            var Q94;
            Q94=makeQuery(id+"F5.boolean.opBoolean","COPY",EDGE,{"derivedFrom":makeQuery(id+"F5.opExtrude","SWEPT_EDGE",EDGE,{"disambiguationData":[OSD([sQuery(id+"F4.wireOp",EDGE,"E29"),sQuery(id+"F4.wireOp",EDGE,"E32.trimOffspring")])]})});
            var Q95;
            Q95=makeQuery(id+"F5.boolean.opBoolean","COPY",EDGE,{"derivedFrom":makeQuery(id+"F5.opExtrude","SWEPT_EDGE",EDGE,{"disambiguationData":[OSD([sQuery(id+"F4.wireOp",EDGE,"E17"),sQuery(id+"F4.wireOp",EDGE,"E19")])]})});
            fillet(context, id + "F7", {"entities" : qUnion([Q0, Q1, Q2, Q3, Q4, Q5, Q6, Q7, Q8, Q9, Q10, Q11, Q12, Q13, Q14, Q15, Q16, Q17, Q18, Q19, Q20, Q21, Q22, Q23, Q24, Q25, Q26, Q27, Q28, Q29, Q30, Q31, Q32, Q33, Q34, Q35, Q36, Q37, Q38, Q39, Q40, Q41, Q42, Q43, Q44, Q45, Q46, Q47, Q48, Q49, Q50, Q51, Q52, Q53, Q54, Q55, Q56, Q57, Q58, Q59, Q60, Q61, Q62, Q63, Q64, Q65, Q66, Q67, Q68, Q69, Q70, Q71, Q72, Q73, Q74, Q75, Q76, Q77, Q78, Q79, Q80, Q81, Q82, Q83, Q84, Q85, Q86, Q87, Q88, Q89, Q90, Q91, Q92, Q93, Q94, Q95]), "radius" : 2 * mm, "tangentPropagation" : true, "allowEdgeOverflow" : false});
        }
    });
